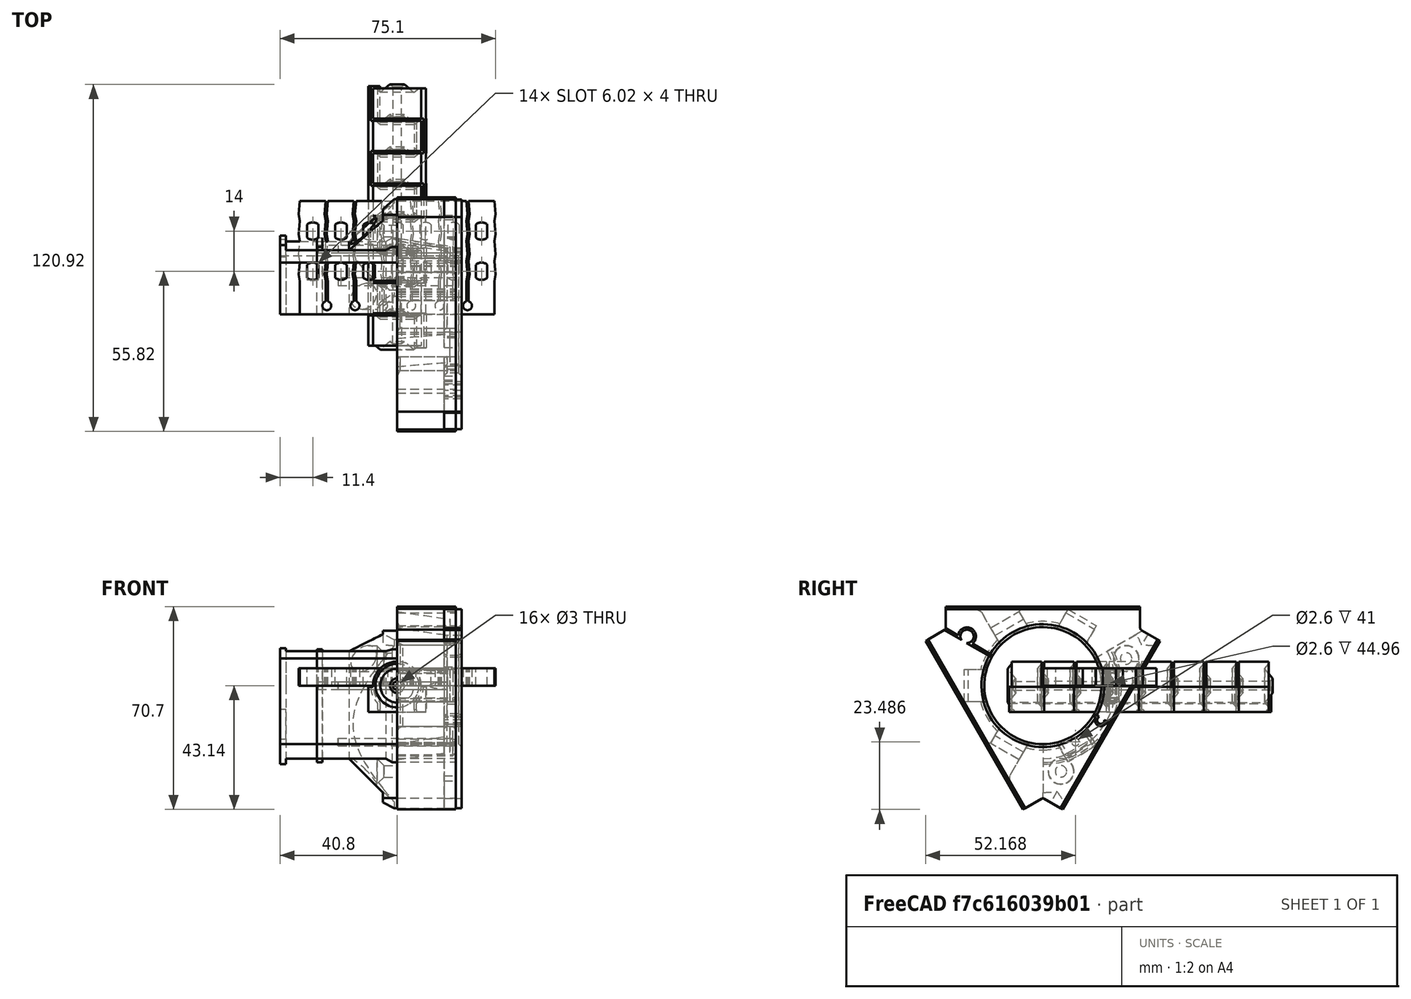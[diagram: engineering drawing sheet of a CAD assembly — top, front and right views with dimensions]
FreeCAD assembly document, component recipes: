
FREECAD ASSEMBLY — COMPONENT RECIPES ("BaseHingeModel_ver1.3_BandOnAxisBander")

This assembly document has 9 components, labeled P0..P8 below (a component is one placed body or linked part). 8 of them carry a construction recipe — the FreeCAD feature program that regenerates the part from scratch, quoted from this document or its linked companion documents; the rest are supplied as boundary geometry only. No exploded tour is included for this assembly.
NOTE — this tour is split across 2 documents so each fits a 32k-token context. This is document 1: the component sections continue in the remaining 1 document, each repeating the header above.
COMPONENT P0 — geometry summary ("Assembly"; no construction recipe available for this part):
  bounding box: 182.8 x 158.8 x 17.6 mm
  tessellated surface: 20,346 triangles
  volume: 11972621413014756431147097229976982929586403496314828412581110393578543582508654598538056830535573487008973004141558221594064665428114596506057430752296960 mm^3 (2342655092617214724371621224931003916189480584224963561102284116985405106658547483193773001758383925594768108753837361044603796868873288666810352140288% of its bounding box)
COMPONENT P1 — recipe-attached ("BaseHingePart", modeled in this document).
Construction recipe (the document's own serialized feature program — sketch geometry with constraints, then the solid features built on it; lengths are millimeters unless a unit is written):

FEATURE [Sketcher::SketchObject] Sketch007  label="RightCylinderScatch"
  FullyConstrained = true
  MapMode = 5
  Support = -> [XY_Plane002]
  expr: Constraints[10] = Spreadsheet.mmDiskHight
  expr: Constraints[11] = Spreadsheet.mmLedgeStep
  expr: Constraints[12] = Spreadsheet.mmLedgeStep * 2
  expr: Constraints[13] = Spreadsheet.mmLedgeStep
  expr: Constraints[14] = Spreadsheet.mmLedgeStep / 2
  expr: Constraints[16] = Spreadsheet.mmDiskLedge
  expr: Constraints[20] = Spreadsheet.mmDiskLedge * 2
  expr: Constraints[21] = Spreadsheet.mmDiskLedge
  expr: Constraints[34] = Spreadsheet.mmAirSpace / 2
  expr: Constraints[35] = Spreadsheet.mmLedgeStep / 2
  sketch-geometry (12):
    g0: LineSegment StartX=0 StartY=10.9 StartZ=0 EndX=0.84 EndY=10.9 EndZ=0
    g1: LineSegment StartX=0.84 StartY=10.9 StartZ=0 EndX=2.52 EndY=12.3 EndZ=0
    g2: LineSegment StartX=2.52 StartY=12.3 StartZ=0 EndX=5.88 EndY=9.5 EndZ=0
    g3: LineSegment StartX=5.88 StartY=9.5 StartZ=0 EndX=7.56 EndY=10.9 EndZ=0
    g4: LineSegment StartX=7.56 StartY=10.9 StartZ=0 EndX=8.4 EndY=10.9 EndZ=0
    g5: LineSegment StartX=5.88 StartY=-1 StartZ=0 EndX=2.52 EndY=1.8 EndZ=0
    g6: LineSegment StartX=2.52 StartY=1.8 StartZ=0 EndX=0.84 EndY=0.4 EndZ=0
    g7: LineSegment StartX=0.84 StartY=0.4 StartZ=0 EndX=0 EndY=0.4 EndZ=0
    g8: LineSegment StartX=0 StartY=0.4 StartZ=0 EndX=0 EndY=10.9 EndZ=0
    g9: LineSegment StartX=8.4 StartY=0.4 StartZ=0 EndX=7.56 EndY=0.4 EndZ=0
    g10: LineSegment StartX=7.56 StartY=0.4 StartZ=0 EndX=5.88 EndY=-1 EndZ=0
    g11: LineSegment StartX=8.4 StartY=10.9 StartZ=0 EndX=8.4 EndY=0.4 EndZ=0
  constraints (38):
    c: PointOnObject(g0,g-2)
    c: Horizontal(g0)
    c: Coincident(g0,g1)
    c: Coincident(g1,g2)
    c: Coincident(g2,g3)
    c: Coincident(g3,g4)
    c: Horizontal(g4)
    c: Coincident(g5,g6)
    c: Horizontal(g7)
    c: Coincident(g7,g8)
    c: DistanceY(g7,g0) = 10.5
    c: DistanceX(g0,g1) = 1.68
    c: DistanceX(g1,g2) = 3.36
    c: DistanceX(g2,g3) = 1.68
    c: DistanceX(g3,g4) = 0.84
    c: Coincident(g6,g7)
    c: DistanceY(g0,g1) = 1.4
    c: Equal(g0,g7)
    c: Equal(g1,g6)
    c: Coincident(g0,g8)
    c: DistanceY(g2,g1) = 2.8
    c: DistanceY(g2,g3) = 1.4
    c: Parallel(g2,g5)
    c: Coincident(g9,g10)
    c: Coincident(g10,g5)
    c: Parallel(g3,g10)
    c: Equal(g4,g9)
    c: Horizontal(g9)
    c: Vertical(g2,g5)
    c: Parallel(g1,g6)
    c: Vertical(g8)
    c: Coincident(g11,g4)
    c: Coincident(g11,g9)
    c: Vertical(g11)
    c: DistanceY(g-1,g7) = 0.4
    c: DistanceX(g-1,g0) = 0.84
    c: DistanceX(g-1,g0) = 0
    c: Vertical(g1,g5)
FEATURE [Sketcher::SketchObject] Sketch011  label="LeftCylinderScatch"
  FullyConstrained = true
  MapMode = 5
  Support = -> [XY_Plane]
  expr: Constraints[10] = Spreadsheet.mmLedgeStep
  expr: Constraints[11] = Spreadsheet.mmLedgeStep * 2
  expr: Constraints[12] = Spreadsheet.mmLedgeStep
  expr: Constraints[13] = Spreadsheet.mmLedgeStep / 2
  expr: Constraints[15] = Spreadsheet.mmDiskLedge
  expr: Constraints[19] = Spreadsheet.mmDiskLedge * 2
  expr: Constraints[20] = Spreadsheet.mmDiskLedge
  expr: Constraints[33] = Spreadsheet.mmAirSpace / 2
  expr: Constraints[34] = Spreadsheet.mmLedgeStep / 2
  expr: Constraints[9] = Spreadsheet.mmDiskHight
  sketch-geometry (12):
    g0: LineSegment StartX=0 StartY=-0.4 StartZ=0 EndX=0.84 EndY=-0.4 EndZ=0
    g1: LineSegment StartX=0.84 StartY=-0.4 StartZ=0 EndX=2.52 EndY=1 EndZ=0
    g2: LineSegment StartX=2.52 StartY=1 StartZ=0 EndX=5.88 EndY=-1.8 EndZ=0
    g3: LineSegment StartX=5.88 StartY=-1.8 StartZ=0 EndX=7.56 EndY=-0.4 EndZ=0
    g4: LineSegment StartX=7.56 StartY=-0.4 StartZ=0 EndX=8.4 EndY=-0.4 EndZ=0
    g5: LineSegment StartX=5.88 StartY=-12.3 StartZ=0 EndX=2.52 EndY=-9.5 EndZ=0
    g6: LineSegment StartX=2.52 StartY=-9.5 StartZ=0 EndX=0.84 EndY=-10.9 EndZ=0
    g7: LineSegment StartX=0.84 StartY=-10.9 StartZ=0 EndX=0 EndY=-10.9 EndZ=0
    g8: LineSegment StartX=0 StartY=-10.9 StartZ=0 EndX=0 EndY=-0.4 EndZ=0
    g9: LineSegment StartX=8.4 StartY=-10.9 StartZ=0 EndX=7.56 EndY=-10.9 EndZ=0
    g10: LineSegment StartX=7.56 StartY=-10.9 StartZ=0 EndX=5.88 EndY=-12.3 EndZ=0
    g11: LineSegment StartX=8.4 StartY=-0.4 StartZ=0 EndX=8.4 EndY=-10.9 EndZ=0
  constraints (36):
    c: Horizontal(g0)
    c: Coincident(g0,g1)
    c: Coincident(g1,g2)
    c: Coincident(g2,g3)
    c: Coincident(g3,g4)
    c: Horizontal(g4)
    c: Coincident(g5,g6)
    c: Horizontal(g7)
    c: Coincident(g7,g8)
    c: DistanceY(g7,g0) = 10.5
    c: DistanceX(g0,g1) = 1.68
    c: DistanceX(g1,g2) = 3.36
    c: DistanceX(g2,g3) = 1.68
    c: DistanceX(g3,g4) = 0.84
    c: Coincident(g6,g7)
    c: DistanceY(g0,g1) = 1.4
    c: Equal(g0,g7)
    c: Equal(g1,g6)
    c: Coincident(g0,g8)
    c: DistanceY(g2,g1) = 2.8
    c: DistanceY(g2,g3) = 1.4
    c: Parallel(g2,g5)
    c: Coincident(g9,g10)
    c: Coincident(g10,g5)
    c: Parallel(g3,g10)
    c: Equal(g4,g9)
    c: Horizontal(g9)
    c: Vertical(g2,g5)
    c: Parallel(g1,g6)
    c: Vertical(g8)
    c: Coincident(g11,g4)
    c: Coincident(g11,g9)
    c: Vertical(g11)
    c: DistanceY(g0,g-1) = 0.4
    c: DistanceX(g-1,g0) = 0.84
    c: DistanceX(g-1,g0) = 0
FEATURE [PartDesign::Revolution] Revolution  label="RightCylinderRevolution"
  Angle = 360
  Axis = (0,1,0)
  Base = (0,0,0)
  Profile = -> Sketch007
  ReferenceAxis = -> Sketch007 [V_Axis]
  Reversed = true
FEATURE [PartDesign::Revolution] Revolution004  label="LeftCylinderRevolution"
  Angle = 360
  Axis = (0,1,0)
  Base = (0,0,0)
  Profile = -> Sketch011
  ReferenceAxis = -> Sketch011 [V_Axis]
  Reversed = true
FEATURE [Sketcher::SketchObject] Sketch013  label="RightCylinderAxisHoleScatch"
  AttachmentOffset = pos=(0,0,1) rot=(0,0,1;0rad)
  FullyConstrained = true
  MapMode = 5
  Placement = pos=(0,-1,-2e-16) rot=(1,0,0;1.5708rad)
  Support = -> [XZ_Plane002]
  expr: .AttachmentOffset.Base.z = Spreadsheet.mmDiskLedge - Spreadsheet.mmAirSpace / 2
  expr: Constraints[1] = Spreadsheet.mmHoleRadius * 2
  sketch-geometry (1):
    g0: Circle CenterX=0 CenterY=0 CenterZ=0 NormalX=0 NormalY=0 NormalZ=1 AngleXU=0 Radius=1.5
  constraints (2):
    c: Coincident(g0,g-1)
    c: Diameter(g0) = 3
FEATURE [PartDesign::Pocket] Pocket001  label="RightCylinderAxisHole"
  BaseFeature = -> Revolution
  Direction = (0,1,2e-16)
  Length = 23.8
  Length2 = 5
  Profile = -> Sketch013
  ReferenceAxis = -> Sketch013 [N_Axis]
  Type = 0
  expr: Length = 2 * Spreadsheet.mmDiskHight + 2 * Spreadsheet.mmDiskLedge
FEATURE [Sketcher::SketchObject] Sketch014  label="LeftCylinderAxisHoleScatch"
  AttachmentOffset = pos=(0,0,-1) rot=(0,0,1;0rad)
  FullyConstrained = true
  MapMode = 5
  Placement = pos=(0,1,2e-16) rot=(1,0,0;1.5708rad)
  Support = -> [XZ_Plane]
  expr: .AttachmentOffset.Base.z = -(Spreadsheet.mmDiskLedge - Spreadsheet.mmAirSpace / 2)
  expr: Constraints[1] = Spreadsheet.mmHoleRadius * 2
  sketch-geometry (1):
    g0: Circle CenterX=0 CenterY=0 CenterZ=0 NormalX=0 NormalY=0 NormalZ=1 AngleXU=0 Radius=1.5
  constraints (2):
    c: Coincident(g0,g-1)
    c: Diameter(g0) = 3
FEATURE [PartDesign::Pocket] Pocket002  label="LeftCylinderAxisHole"
  BaseFeature = -> Revolution004
  Direction = (0,1,2e-16)
  Length = 21
  Length2 = 5
  Profile = -> Sketch014
  ReferenceAxis = -> Sketch014 [N_Axis]
  Reversed = true
  Type = 0
  expr: Length = Spreadsheet.mmDiskHight * 2
FEATURE [Sketcher::SketchObject] Sketch023  label="RightCylinderConnectedWingScatch"
  AttachmentOffset = pos=(0,0,-0.4) rot=(0,0,1;0rad)
  FullyConstrained = false
  MapMode = 5
  Placement = pos=(0,0.4,1e-16) rot=(1,0,0;1.5708rad)
  Support = -> [XZ_Plane002]
  expr: .AttachmentOffset.Base.z = -Spreadsheet.mmAirSpace / 2
  expr: Constraints[11] = Spreadsheet.mmHingeRadius + Spreadsheet.mmAirSpace
  expr: Constraints[17] = Spreadsheet.mmHingeRadius + Spreadsheet.mmAirSpace
  expr: Constraints[4] = Spreadsheet.mmHingeRadius * 2
  expr: Constraints[7] = Spreadsheet.mmHingeRadius / 5
  expr: Constraints[8] = Spreadsheet.mmAirSpace / 2
  sketch-geometry (9):
    g0: LineSegment StartX=-5.9397 StartY=-9.2 StartZ=0 EndX=10.0705 EndY=-9.2 EndZ=0
    g1: LineSegment StartX=10.0705 StartY=-9.2 StartZ=0 EndX=10.0705 EndY=-0.4 EndZ=0
    g2: LineSegment StartX=10.0705 StartY=-0.4 StartZ=0 EndX=8.39047 EndY=-0.4 EndZ=0
    g3: ArcOfCircle CenterX=0 CenterY=9e-16 CenterZ=0 NormalX=0 NormalY=0 NormalZ=1 AngleXU=0 Radius=8.4 StartAngle=3.92699 EndAngle=6.23555
    g4: LineSegment StartX=-10.8949 StartY=25.2528 StartZ=0 EndX=-10.8949 EndY=-29.472 EndZ=0
    g5: LineSegment StartX=0 StartY=0 StartZ=0 EndX=8.39047 EndY=-0.4 EndZ=0
    g6: LineSegment StartX=-5.9397 StartY=-5.9397 StartZ=0 EndX=-5.9397 EndY=-9.2 EndZ=0
    g7: LineSegment StartX=0 StartY=9e-16 StartZ=0 EndX=-20.2547 EndY=-20.2547 EndZ=0
    g8: LineSegment StartX=-5.9397 StartY=-5.9397 StartZ=0 EndX=-5.9397 EndY=-9.42884 EndZ=0
  constraints (24):
    c: Coincident(g0,g1)
    c: Vertical(g1)
    c: Horizontal(g2)
    c: Vertical(g4)
    c: Diameter(g3) = 16.8
    c: Coincident(g2,g1)
    c: Coincident(g5,g2)
    c: DistanceX(g2,g2) = 1.68
    c: DistanceY(g1,g-1) = 0.4
    c: Coincident(g3,g6)
    c: Coincident(g3,g2)
    c: DistanceY(g0,g3) = 9.2
    c: PointOnObject(g3,g7)
    c: Coincident(g7,g3)
    c: Angle(g-2,g7) = 2.35619
    c: PointOnObject(g3,g-2)
    c: Horizontal(g0)
    c: DistanceY(g0,g-1) = 9.2
    c: Vertical(g8)
    c: PointOnObject(g8,g7)
    c: PointOnObject(g8,g3)
    c: PointOnObject(g6,g8)
    c: PointOnObject(g0,g8)
    c: PointOnObject(g6,g0)
FEATURE [PartDesign::Pad] Pad008  label="RightCylinderConnectedWingBody"
  BaseFeature = -> Pocket001
  Direction = (0,-1,-2e-16)
  Length = 10.5
  Length2 = 10
  Profile = -> Sketch023
  ReferenceAxis = -> Sketch023 [N_Axis]
  Reversed = true
  Type = 0
  expr: Length = Spreadsheet.mmDiskHight
FEATURE [Sketcher::SketchObject] Sketch024  label="RightCylinderDisconnectedWingScatch"
  AttachmentOffset = pos=(0,0,0.4) rot=(0,0,1;0rad)
  FullyConstrained = false
  MapMode = 5
  Placement = pos=(0,-0.4,-1e-16) rot=(1,0,0;1.5708rad)
  Support = -> [XZ_Plane002]
  expr: .AttachmentOffset.Base.z = Spreadsheet.mmAirSpace / 2
  expr: Constraints[10] = Spreadsheet.mmHingeRadius * 6 / 5
  expr: Constraints[14] = (Spreadsheet.mmHingeRadius + Spreadsheet.mmAirSpace) * 2
  expr: Constraints[18] = Spreadsheet.mmAirSpace
  expr: Constraints[26] = Spreadsheet.mmAirSpace
  expr: Constraints[29] = Spreadsheet.mmHingeRadius * 2
  expr: Constraints[2] = (Spreadsheet.mmHingeRadius + Spreadsheet.mmAirSpace) * 2
  expr: Constraints[8] = Spreadsheet.mmHingeRadius + Spreadsheet.mmAirSpace
  expr: Constraints[9] = Spreadsheet.mmAirSpace / 2
  sketch-geometry (12):
    g0: Circle CenterX=0 CenterY=0 CenterZ=0 NormalX=0 NormalY=0 NormalZ=1 AngleXU=0 Radius=9.2
    g1: LineSegment StartX=-5.9397 StartY=-5.9397 StartZ=0 EndX=-5.9397 EndY=-9.59435 EndZ=0
    g2: LineSegment StartX=-10.08 StartY=-0.4 StartZ=0 EndX=-10.08 EndY=-9.2 EndZ=0
    g3: LineSegment StartX=-10.08 StartY=-9.2 StartZ=0 EndX=-5.9397 EndY=-9.2 EndZ=0
    g4: LineSegment StartX=-6.7397 StartY=-8.4 StartZ=0 EndX=-6.7397 EndY=-6.26231 EndZ=0
    g5: LineSegment StartX=-9.1913 StartY=-0.4 StartZ=0 EndX=-10.08 EndY=-0.4 EndZ=0
    g6: LineSegment StartX=0 StartY=0 StartZ=0 EndX=-7.18968 EndY=-7.18968 EndZ=0
    g7: ArcOfCircle CenterX=0 CenterY=0 CenterZ=0 NormalX=0 NormalY=0 NormalZ=1 AngleXU=0 Radius=9.2 StartAngle=3.18508 EndAngle=3.89029
    g8: LineSegment StartX=-6.7397 StartY=-9.55843 StartZ=0 EndX=-6.7397 EndY=-4.9559 EndZ=0
    g9: LineSegment StartX=-6.7397 StartY=-8.4 StartZ=0 EndX=-5.9397 EndY=-8.4 EndZ=0
    g10: LineSegment StartX=-5.9397 StartY=-8.4 StartZ=0 EndX=-5.9397 EndY=-9.2 EndZ=0
    g11: Circle CenterX=0 CenterY=0 CenterZ=0 NormalX=0 NormalY=0 NormalZ=1 AngleXU=0 Radius=8.4
  constraints (33):
    c: Coincident(g0,g-1)
    c: Vertical(g1)
    c: Diameter(g0) = 18.4
    c: Vertical(g2)
    c: Coincident(g2,g3)
    c: Horizontal(g3)
    c: Coincident(g5,g2)
    c: Horizontal(g5)
    c: DistanceY(g2,g-1) = 9.2
    c: DistanceY(g2,g-1) = 0.4
    c: DistanceX(g2,g0) = 10.08
    c: Coincident(g6,g0)
    c: Angle(g-2,g6) = 2.35619
    c: Coincident(g7,g0)
    c: Diameter(g7) = 18.4
    c: Coincident(g7,g4)
    c: Coincident(g7,g5)
    c: Vertical(g8)
    c: DistanceX(g8,g1) = 0.8
    c: Coincident(g4,g9)
    c: PointOnObject(g9,g1)
    c: Horizontal(g9)
    c: Coincident(g9,g10)
    c: PointOnObject(g10,g1)
    c: PointOnObject(g3,g1)
    c: PointOnObject(g10,g3)
    c: DistanceY(g3,g9) = 0.8
    c: PointOnObject(g4,g8)
    c: Coincident(g11,g7)
    c: Diameter(g11) = 16.8
    c: PointOnObject(g1,g11)
    c: PointOnObject(g1,g6)
    c: PointOnObject(g4,g8)
FEATURE [PartDesign::Pad] Pad009  label="RightCylinderDisconnectedWingBody"
  BaseFeature = -> Pad008
  Direction = (0,-1,-2e-16)
  Length = 12.1
  Length2 = 10
  Profile = -> Sketch024
  ReferenceAxis = -> Sketch024 [N_Axis]
  Reversed = true
  Type = 0
  expr: Length = Spreadsheet.mmDiskHight + Spreadsheet.mmAirSpace * 2
FEATURE [Sketcher::SketchObject] Sketch025  label="LeftCylinderConnectedWingScatch"
  AttachmentOffset = pos=(0,0,0.4) rot=(0,0,1;0rad)
  FullyConstrained = false
  MapMode = 5
  Placement = pos=(0,-0.4,-1e-16) rot=(1,0,0;1.5708rad)
  Support = -> [XZ_Plane]
  expr: .AttachmentOffset.Base.z = Spreadsheet.mmAirSpace / 2
  expr: Constraints[10] = Spreadsheet.mmAirSpace / 2
  expr: Constraints[11] = Spreadsheet.mmHingeRadius + Spreadsheet.mmAirSpace
  expr: Constraints[15] = Spreadsheet.mmHingeRadius * 2
  expr: Constraints[2] = Spreadsheet.mmHingeRadius * 2
  expr: Constraints[9] = Spreadsheet.mmHingeRadius * 6 / 5
  sketch-geometry (8):
    g0: LineSegment StartX=0 StartY=0 StartZ=0 EndX=8.8497 EndY=-8.8497 EndZ=0
    g1: Circle CenterX=0 CenterY=0 CenterZ=0 NormalX=0 NormalY=0 NormalZ=1 AngleXU=0 Radius=8.4
    g2: LineSegment StartX=-10.08 StartY=-0.4 StartZ=0 EndX=-10.08 EndY=-9.2 EndZ=0
    g3: LineSegment StartX=-10.08 StartY=-9.2 StartZ=0 EndX=5.9397 EndY=-9.2 EndZ=0
    g4: LineSegment StartX=5.9397 StartY=-9.2 StartZ=0 EndX=5.9397 EndY=-5.9397 EndZ=0
    g5: LineSegment StartX=-8.39047 StartY=-0.4 StartZ=0 EndX=-10.08 EndY=-0.4 EndZ=0
    g6: ArcOfCircle CenterX=0 CenterY=0 CenterZ=0 NormalX=0 NormalY=0 NormalZ=1 AngleXU=0 Radius=8.4 StartAngle=3.18923 EndAngle=5.49779
    g7: LineSegment StartX=5.9397 StartY=-5.9397 StartZ=0 EndX=5.9397 EndY=-9.58153 EndZ=0
  constraints (24):
    c: Coincident(g0,g-1)
    c: Coincident(g1,g0)
    c: Diameter(g1) = 16.8
    c: Vertical(g2)
    c: Coincident(g2,g3)
    c: Horizontal(g3)
    c: Coincident(g5,g2)
    c: Horizontal(g5)
    c: PointOnObject(g5,g1)
    c: DistanceX(g2,g0) = 10.08
    c: DistanceY(g2,g-1) = 0.4
    c: DistanceY(g2,g-1) = 9.2
    c: Angle(g0,g-2) = 2.35619
    c: PointOnObject(g4,g0)
    c: Coincident(g6,g0)
    c: Diameter(g6) = 16.8
    c: Coincident(g6,g5)
    c: Coincident(g6,g4)
    c: Vertical(g7)
    c: PointOnObject(g7,g1)
    c: PointOnObject(g7,g0)
    c: PointOnObject(g4,g7)
    c: PointOnObject(g3,g7)
    c: PointOnObject(g4,g3)
FEATURE [PartDesign::Pad] Pad010  label="LeftCylinderConnectedWingBody"
  BaseFeature = -> Pocket002
  Direction = (0,-1,-2e-16)
  Length = 10.5
  Length2 = 10
  Profile = -> Sketch025
  ReferenceAxis = -> Sketch025 [N_Axis]
  Type = 0
  expr: Length = Spreadsheet.mmDiskHight
FEATURE [Sketcher::SketchObject] Sketch026  label="LeftCylinderDisconnectedWingScatch"
  AttachmentOffset = pos=(0,0,-0.4) rot=(0,0,1;0rad)
  FullyConstrained = false
  MapMode = 5
  Placement = pos=(0,0.4,1e-16) rot=(1,0,0;1.5708rad)
  Support = -> [XZ_Plane]
  expr: .AttachmentOffset.Base.z = -Spreadsheet.mmAirSpace / 2
  expr: Constraints[10] = Spreadsheet.mmHingeRadius + Spreadsheet.mmAirSpace
  expr: Constraints[16] = Spreadsheet.mmAirSpace
  expr: Constraints[18] = (Spreadsheet.mmHingeRadius + Spreadsheet.mmAirSpace) * 2
  expr: Constraints[26] = Spreadsheet.mmAirSpace
  expr: Constraints[29] = Spreadsheet.mmHingeRadius * 2
  expr: Constraints[2] = (Spreadsheet.mmHingeRadius + Spreadsheet.mmAirSpace) * 2
  expr: Constraints[8] = Spreadsheet.mmAirSpace / 2
  expr: Constraints[9] = Spreadsheet.mmHingeRadius / 5 * 6
  sketch-geometry (12):
    g0: LineSegment StartX=0 StartY=0 StartZ=0 EndX=9.28474 EndY=-9.28474 EndZ=0
    g1: ArcOfCircle CenterX=0 CenterY=0 CenterZ=0 NormalX=0 NormalY=0 NormalZ=1 AngleXU=0 Radius=9.2 StartAngle=5.53449 EndAngle=6.23969
    g2: LineSegment StartX=9.1913 StartY=-0.4 StartZ=0 EndX=10.08 EndY=-0.4 EndZ=0
    g3: LineSegment StartX=10.08 StartY=-0.4 StartZ=0 EndX=10.08 EndY=-9.2 EndZ=0
    g4: LineSegment StartX=10.08 StartY=-9.2 StartZ=0 EndX=5.9397 EndY=-9.2 EndZ=0
    g5: LineSegment StartX=6.7397 StartY=-8.4 StartZ=0 EndX=6.7397 EndY=-6.26231 EndZ=0
    g6: LineSegment StartX=5.9397 StartY=-5.9397 StartZ=0 EndX=5.9397 EndY=-9.17966 EndZ=0
    g7: LineSegment StartX=6.7397 StartY=-5.451 StartZ=0 EndX=6.7397 EndY=-9.15329 EndZ=0
    g8: Circle CenterX=0 CenterY=0 CenterZ=0 NormalX=0 NormalY=0 NormalZ=1 AngleXU=0 Radius=9.2
    g9: LineSegment StartX=6.7397 StartY=-8.4 StartZ=0 EndX=5.9397 EndY=-8.4 EndZ=0
    g10: LineSegment StartX=5.9397 StartY=-8.4 StartZ=0 EndX=5.9397 EndY=-9.2 EndZ=0
    g11: Circle CenterX=0 CenterY=0 CenterZ=0 NormalX=0 NormalY=0 NormalZ=1 AngleXU=0 Radius=8.4
  constraints (33):
    c: Coincident(g0,g-1)
    c: Coincident(g1,g0)
    c: Diameter(g1) = 18.4
    c: Horizontal(g2)
    c: Coincident(g2,g3)
    c: Vertical(g3)
    c: Coincident(g3,g4)
    c: Horizontal(g4)
    c: DistanceY(g2,g-1) = 0.4
    c: DistanceX(g-1,g2) = 10.08
    c: DistanceY(g3,g-1) = 9.2
    c: Angle(g0,g-2) = 2.35619
    c: Coincident(g1,g2)
    c: Coincident(g1,g5)
    c: Vertical(g6)
    c: Vertical(g7)
    c: DistanceX(g6,g7) = 0.8
    c: Coincident(g8,g1)
    c: Diameter(g8) = 18.4
    c: PointOnObject(g5,g7)
    c: Coincident(g5,g9)
    c: PointOnObject(g9,g6)
    c: Horizontal(g9)
    c: Coincident(g9,g10)
    c: PointOnObject(g10,g6)
    c: PointOnObject(g4,g6)
    c: DistanceY(g4,g9) = 0.8
    c: PointOnObject(g10,g4)
    c: Coincident(g11,g1)
    c: Diameter(g11) = 16.8
    c: PointOnObject(g6,g11)
    c: PointOnObject(g6,g0)
    c: PointOnObject(g1,g7)
FEATURE [PartDesign::Pad] Pad011  label="LeftCylinderDisconnectedWingBody"
  BaseFeature = -> Pad010
  Direction = (0,-1,-2e-16)
  Length = 12.1
  Length2 = 10
  Profile = -> Sketch026
  ReferenceAxis = -> Sketch026 [N_Axis]
  Type = 0
  expr: Length = Spreadsheet.mmDiskHight + Spreadsheet.mmAirSpace * 2
FEATURE [Sketcher::SketchObject] Sketch046  label="LeftCylinderSeparatorScatch"
  AttachmentOffset = pos=(0,0,-0.4) rot=(0,0,1;0rad)
  FullyConstrained = false
  MapMode = 5
  Placement = pos=(0,0.4,1e-16) rot=(1,0,0;1.5708rad)
  Support = -> [XZ_Plane]
  expr: .AttachmentOffset.Base.z = -Spreadsheet.mmAirSpace / 2
  expr: Constraints[14] = Spreadsheet.mmAirSpace
  expr: Constraints[15] = Spreadsheet.mmHingeRadius * 2
  expr: Constraints[2] = Spreadsheet.mmHingeRadius + Spreadsheet.mmAirSpace
  expr: Constraints[6] = Spreadsheet.mmAirSpace
  expr: Constraints[7] = (Spreadsheet.mmHingeRadius + Spreadsheet.mmAirSpace) * 2
  sketch-geometry (9):
    g0: LineSegment StartX=0 StartY=0 StartZ=0 EndX=9.28922 EndY=-9.28922 EndZ=0
    g1: LineSegment StartX=6.7397 StartY=-9.2 StartZ=0 EndX=5.9397 EndY=-9.2 EndZ=0
    g2: LineSegment StartX=6.7397 StartY=-8.4 StartZ=0 EndX=6.7397 EndY=-9.2 EndZ=0
    g3: LineSegment StartX=5.9397 StartY=-5.9397 StartZ=0 EndX=5.9397 EndY=-8.88748 EndZ=0
    g4: LineSegment StartX=6.7397 StartY=-5.40605 StartZ=0 EndX=6.7397 EndY=-8.88997 EndZ=0
    g5: Circle CenterX=0 CenterY=0 CenterZ=0 NormalX=0 NormalY=0 NormalZ=1 AngleXU=0 Radius=9.2
    g6: LineSegment StartX=6.7397 StartY=-8.4 StartZ=0 EndX=5.9397 EndY=-8.4 EndZ=0
    g7: LineSegment StartX=5.9397 StartY=-8.4 StartZ=0 EndX=5.9397 EndY=-9.2 EndZ=0
    g8: Circle CenterX=0 CenterY=0 CenterZ=0 NormalX=0 NormalY=0 NormalZ=1 AngleXU=0 Radius=8.4
  constraints (23):
    c: Coincident(g0,g-1)
    c: Horizontal(g1)
    c: DistanceY(g1,g-1) = 9.2
    c: Angle(g0,g-2) = 2.35619
    c: Vertical(g3)
    c: Vertical(g4)
    c: DistanceX(g3,g4) = 0.8
    c: Diameter(g5) = 18.4
    c: PointOnObject(g2,g4)
    c: Coincident(g2,g6)
    c: PointOnObject(g6,g3)
    c: Horizontal(g6)
    c: Coincident(g6,g7)
    c: PointOnObject(g7,g3)
    c: DistanceY(g1,g6) = 0.8
    c: Diameter(g8) = 16.8
    c: PointOnObject(g3,g8)
    c: PointOnObject(g3,g0)
    c: PointOnObject(g1,g4)
    c: Coincident(g2,g1)
    c: Coincident(g0,g8)
    c: Coincident(g0,g5)
    c: Coincident(g7,g1)
FEATURE [PartDesign::Pocket] Pocket004  label="LeftCylinderSeparator"
  BaseFeature = -> Pad011
  Direction = (0,1,2e-16)
  Length = 10.5
  Length2 = 5
  Profile = -> Sketch046
  ReferenceAxis = -> Sketch046 [N_Axis]
  Reversed = true
  Type = 0
  expr: Length = Spreadsheet.mmDiskHight
FEATURE [PartDesign::Body] Body  label="LeftCylinder"
  Group = -> [Sketch011,Revolution004,Sketch014,Pocket002,Sketch025,Pad010,Sketch026,Pad011,Sketch046,Pocket004]
  Origin = -> Origin
  Tip = -> Pocket004
FEATURE [Sketcher::SketchObject] Sketch047  label="RightCylinderSeparatorScatch"
  AttachmentOffset = pos=(0,0,0.4) rot=(0,0,1;0rad)
  FullyConstrained = false
  MapMode = 5
  Placement = pos=(0,-0.4,-1e-16) rot=(1,0,0;1.5708rad)
  Support = -> [XZ_Plane002]
  expr: .AttachmentOffset.Base.z = Spreadsheet.mmAirSpace / 2
  expr: Constraints[15] = Spreadsheet.mmAirSpace
  expr: Constraints[17] = Spreadsheet.mmHingeRadius * 2
  expr: Constraints[2] = (Spreadsheet.mmHingeRadius + Spreadsheet.mmAirSpace) * 2
  expr: Constraints[4] = Spreadsheet.mmHingeRadius + Spreadsheet.mmAirSpace
  expr: Constraints[8] = Spreadsheet.mmAirSpace
  sketch-geometry (9):
    g0: Circle CenterX=0 CenterY=0 CenterZ=0 NormalX=0 NormalY=0 NormalZ=1 AngleXU=0 Radius=9.2
    g1: LineSegment StartX=-5.9397 StartY=-5.9397 StartZ=0 EndX=-5.9397 EndY=-9.59435 EndZ=0
    g2: LineSegment StartX=-6.7397 StartY=-9.2 StartZ=0 EndX=-5.9397 EndY=-9.2 EndZ=0
    g3: LineSegment StartX=0 StartY=0 StartZ=0 EndX=-7.19425 EndY=-7.19425 EndZ=0
    g4: LineSegment StartX=-6.7397 StartY=-9.55843 StartZ=0 EndX=-6.7397 EndY=-4.9559 EndZ=0
    g5: LineSegment StartX=-6.7397 StartY=-8.4 StartZ=0 EndX=-5.9397 EndY=-8.4 EndZ=0
    g6: LineSegment StartX=-5.9397 StartY=-8.4 StartZ=0 EndX=-5.9397 EndY=-9.2 EndZ=0
    g7: Circle CenterX=0 CenterY=0 CenterZ=0 NormalX=0 NormalY=0 NormalZ=1 AngleXU=0 Radius=8.4
    g8: LineSegment StartX=-6.7397 StartY=-8.4 StartZ=0 EndX=-6.7397 EndY=-9.2 EndZ=0
  constraints (24):
    c: Coincident(g0,g-1)
    c: Vertical(g1)
    c: Diameter(g0) = 18.4
    c: Horizontal(g2)
    c: DistanceY(g2,g-1) = 9.2
    c: Coincident(g3,g0)
    c: Angle(g-2,g3) = 2.35619
    c: Vertical(g4)
    c: DistanceX(g4,g1) = 0.8
    c: PointOnObject(g5,g1)
    c: Horizontal(g5)
    c: Coincident(g5,g6)
    c: PointOnObject(g6,g1)
    c: PointOnObject(g2,g1)
    c: PointOnObject(g6,g2)
    c: DistanceY(g2,g5) = 0.8
    c: PointOnObject(g5,g4)
    c: Diameter(g7) = 16.8
    c: PointOnObject(g1,g7)
    c: PointOnObject(g1,g3)
    c: PointOnObject(g2,g4)
    c: Coincident(g8,g5)
    c: Coincident(g8,g2)
    c: Coincident(g0,g7)
FEATURE [PartDesign::Pocket] Pocket005  label="RightCylinderSeparator"
  BaseFeature = -> Pad009
  Direction = (0,1,2e-16)
  Length = 10.5
  Length2 = 5
  Profile = -> Sketch047
  ReferenceAxis = -> Sketch047 [N_Axis]
  Type = 0
  expr: Length = Spreadsheet.mmDiskHight
FEATURE [PartDesign::Body] Body001  label="RightCylinder"
  Group = -> [Sketch007,Revolution,Sketch013,Pocket001,Sketch023,Pad008,Sketch024,Pad009,Sketch047,Pocket005]
  Origin = -> Origin002
  Tip = -> Pocket005
COMPONENT P2 — recipe-attached ("BeamFixatoPart", modeled in this document).
Construction recipe (the document's own serialized feature program — sketch geometry with constraints, then the solid features built on it; lengths are millimeters unless a unit is written):

FEATURE [Sketcher::SketchObject] Sketch022  label="FixatorBodySketch"
  FullyConstrained = false
  MapMode = 5
  Support = -> [XY_Plane005]
  expr: Constraints[143] = Spreadsheet.mmCellWall
  expr: Constraints[144] = Spreadsheet.mmCellWall
  expr: Constraints[145] = Spreadsheet.mmCellWall
  expr: Constraints[146] = Spreadsheet.mmCellWidth
  expr: Constraints[147] = Spreadsheet.mmCellWidth
  expr: Constraints[148] = Spreadsheet.mmCellWidth
  expr: Constraints[169] = Spreadsheet.mmCommonBaseLenght
  expr: Constraints[170] = Spreadsheet.mmToothStep
  expr: Constraints[171] = Spreadsheet.mmToothStep
  expr: Constraints[172] = Spreadsheet.mmToothStep
  expr: Constraints[173] = Spreadsheet.mmToothStep
  expr: Constraints[174] = Spreadsheet.mmToothStep
  expr: Constraints[183] = Spreadsheet.mmCellWall * 3
  expr: Constraints[184] = Spreadsheet.mmCellWall * 3
  expr: Constraints[185] = Spreadsheet.mmCellWall * 3
  expr: Constraints[186] = Spreadsheet.mmCellWall * 3
  expr: Constraints[425] = Spreadsheet.mmFirstCircleArcToBase
  expr: Constraints[435] = Spreadsheet.mmCellWall / 2
  expr: Constraints[464] = Spreadsheet.mmCellWidth + Spreadsheet.mmCellWall
  expr: Constraints[5] = Spreadsheet.mmBaseWidth
  expr: Constraints[6] = Spreadsheet.mmBaseEnd
  sketch-geometry (155):
    g0: LineSegment StartX=-33.9 StartY=0 StartZ=0 EndX=-33.9 EndY=39.5 EndZ=0
    g1: LineSegment StartX=-33.9 StartY=39.5 StartZ=0 EndX=33.9 EndY=39.5 EndZ=0
    g2: LineSegment StartX=33.9 StartY=39.5 StartZ=0 EndX=33.9 EndY=0 EndZ=0
    g3: LineSegment StartX=-73.1099 StartY=25.5 StartZ=0 EndX=65.6354 EndY=25.5 EndZ=0
    g4: LineSegment StartX=-33.9 StartY=0 StartZ=0 EndX=-33.9 EndY=11.5 EndZ=0
    g5: LineSegment StartX=-33.9 StartY=11.5 StartZ=0 EndX=-34.3 EndY=13.9 EndZ=0
    g6: LineSegment StartX=-34.3 StartY=13.9 StartZ=0 EndX=-33.9 EndY=18.5 EndZ=0
    g7: LineSegment StartX=-33.9 StartY=18.5 StartZ=0 EndX=-34.3 EndY=20.9 EndZ=0
    g8: LineSegment StartX=-34.3 StartY=20.9 StartZ=0 EndX=-33.9 EndY=25.5 EndZ=0
    g9: LineSegment StartX=-33.9 StartY=25.5 StartZ=0 EndX=-34.3 EndY=27.9 EndZ=0
    g10: LineSegment StartX=-34.3 StartY=27.9 StartZ=0 EndX=-33.9 EndY=32.5 EndZ=0
    g11: LineSegment StartX=-33.9 StartY=32.5 StartZ=0 EndX=-34.3 EndY=34.9 EndZ=0
    g12: LineSegment StartX=-34.3 StartY=34.9 StartZ=0 EndX=-33.9 EndY=39.5 EndZ=0
    g13: LineSegment StartX=-33.9 StartY=39.5 StartZ=0 EndX=-24.9 EndY=39.5 EndZ=0
    g14: LineSegment StartX=-24.9 StartY=39.5 StartZ=0 EndX=-25.3 EndY=34.9 EndZ=0
    g15: LineSegment StartX=-25.3 StartY=34.9 StartZ=0 EndX=-24.9 EndY=32.5 EndZ=0
    g16: LineSegment StartX=-24.9 StartY=32.5 StartZ=0 EndX=-25.3 EndY=27.9 EndZ=0
    g17: LineSegment StartX=-25.3 StartY=27.9 StartZ=0 EndX=-24.9 EndY=25.5 EndZ=0
    g18: LineSegment StartX=-24.9 StartY=25.5 StartZ=0 EndX=-25.3 EndY=20.9 EndZ=0
    g19: LineSegment StartX=-25.3 StartY=20.9 StartZ=0 EndX=-24.9 EndY=18.5 EndZ=0
    g20: LineSegment StartX=-24.9 StartY=18.5 StartZ=0 EndX=-25.3 EndY=13.9 EndZ=0
    g21: LineSegment StartX=-25.3 StartY=13.9 StartZ=0 EndX=-24.9 EndY=11.5 EndZ=0
    g22: LineSegment StartX=-24.9 StartY=11.5 StartZ=0 EndX=-24.9 EndY=4.5 EndZ=0
    g23: LineSegment StartX=-24.1 StartY=4.5 StartZ=0 EndX=-24.1 EndY=11.5 EndZ=0
    g24: LineSegment StartX=-24.1 StartY=11.5 StartZ=0 EndX=-24.5 EndY=13.9 EndZ=0
    g25: LineSegment StartX=-24.5 StartY=13.9 StartZ=0 EndX=-24.1 EndY=18.5 EndZ=0
    g26: LineSegment StartX=-24.1 StartY=18.5 StartZ=0 EndX=-24.5 EndY=20.9 EndZ=0
    g27: LineSegment StartX=-24.5 StartY=20.9 StartZ=0 EndX=-24.1 EndY=25.5 EndZ=0
    g28: LineSegment StartX=-24.1 StartY=25.5 StartZ=0 EndX=-24.5 EndY=27.9 EndZ=0
    g29: LineSegment StartX=-24.5 StartY=27.9 StartZ=0 EndX=-24.1 EndY=32.5 EndZ=0
    g30: LineSegment StartX=-24.1 StartY=32.5 StartZ=0 EndX=-24.5 EndY=34.9 EndZ=0
    g31: LineSegment StartX=-24.5 StartY=34.9 StartZ=0 EndX=-24.1 EndY=39.5 EndZ=0
    g32: LineSegment StartX=-24.1 StartY=39.5 StartZ=0 EndX=-15.1 EndY=39.5 EndZ=0
    g33: LineSegment StartX=-15.1 StartY=39.5 StartZ=0 EndX=-15.5 EndY=34.9 EndZ=0
    g34: LineSegment StartX=-15.5 StartY=34.9 StartZ=0 EndX=-15.1 EndY=32.5 EndZ=0
    g35: LineSegment StartX=-15.1 StartY=32.5 StartZ=0 EndX=-15.5 EndY=27.9 EndZ=0
    g36: LineSegment StartX=-15.5 StartY=27.9 StartZ=0 EndX=-15.1 EndY=25.5 EndZ=0
    g37: LineSegment StartX=-15.1 StartY=25.5 StartZ=0 EndX=-15.5 EndY=20.9 EndZ=0
    g38: LineSegment StartX=-15.5 StartY=20.9 StartZ=0 EndX=-15.1 EndY=18.5 EndZ=0
    g39: LineSegment StartX=-15.1 StartY=18.5 StartZ=0 EndX=-15.5 EndY=13.9 EndZ=0
    g40: LineSegment StartX=-15.5 StartY=13.9 StartZ=0 EndX=-15.1 EndY=11.5 EndZ=0
    g41: LineSegment StartX=-15.1 StartY=11.5 StartZ=0 EndX=-15.1 EndY=4.5 EndZ=0
    g42: LineSegment StartX=-14.3 StartY=4.5 StartZ=0 EndX=-14.3 EndY=11.5 EndZ=0
    g43: LineSegment StartX=-14.3 StartY=11.5 StartZ=0 EndX=-14.7 EndY=13.9 EndZ=0
    g44: LineSegment StartX=-14.7 StartY=13.9 StartZ=0 EndX=-14.3 EndY=18.5 EndZ=0
    g45: LineSegment StartX=-14.3 StartY=18.5 StartZ=0 EndX=-14.7 EndY=20.9 EndZ=0
    g46: LineSegment StartX=-14.7 StartY=20.9 StartZ=0 EndX=-14.3 EndY=25.5 EndZ=0
    g47: LineSegment StartX=-14.3 StartY=25.5 StartZ=0 EndX=-14.7 EndY=27.9 EndZ=0
    g48: LineSegment StartX=-14.7 StartY=27.9 StartZ=0 EndX=-14.3 EndY=32.5 EndZ=0
    g49: LineSegment StartX=-14.3 StartY=32.5 StartZ=0 EndX=-14.7 EndY=34.9 EndZ=0
    g50: LineSegment StartX=-14.7 StartY=34.9 StartZ=0 EndX=-14.3 EndY=39.5 EndZ=0
    g51: LineSegment StartX=-14.3 StartY=39.5 StartZ=0 EndX=-5.3 EndY=39.5 EndZ=0
    g52: LineSegment StartX=-5.3 StartY=39.5 StartZ=0 EndX=-5.7 EndY=34.9 EndZ=0
    g53: LineSegment StartX=-5.7 StartY=34.9 StartZ=0 EndX=-5.3 EndY=32.5 EndZ=0
    g54: LineSegment StartX=-5.3 StartY=32.5 StartZ=0 EndX=-5.7 EndY=27.9 EndZ=0
    g55: LineSegment StartX=-5.7 StartY=27.9 StartZ=0 EndX=-5.3 EndY=25.5 EndZ=0
    g56: LineSegment StartX=-5.3 StartY=25.5 StartZ=0 EndX=-5.7 EndY=20.9 EndZ=0
    g57: LineSegment StartX=-5.7 StartY=20.9 StartZ=0 EndX=-5.3 EndY=18.5 EndZ=0
    g58: LineSegment StartX=-5.3 StartY=18.5 StartZ=0 EndX=-5.7 EndY=13.9 EndZ=0
    g59: LineSegment StartX=-5.7 StartY=13.9 StartZ=0 EndX=-5.3 EndY=11.5 EndZ=0
    g60: LineSegment StartX=-5.3 StartY=11.5 StartZ=0 EndX=-5.3 EndY=4.5 EndZ=0
    g61: LineSegment StartX=-4.5 StartY=4.5 StartZ=0 EndX=-4.5 EndY=11.5 EndZ=0
    g62: LineSegment StartX=-4.5 StartY=11.5 StartZ=0 EndX=-4.9 EndY=13.9 EndZ=0
    g63: LineSegment StartX=-4.9 StartY=13.9 StartZ=0 EndX=-4.5 EndY=18.5 EndZ=0
    g64: LineSegment StartX=-4.5 StartY=18.5 StartZ=0 EndX=-4.9 EndY=20.9 EndZ=0
    g65: LineSegment StartX=-4.9 StartY=20.9 StartZ=0 EndX=-4.5 EndY=25.5 EndZ=0
    g66: LineSegment StartX=-4.5 StartY=25.5 StartZ=0 EndX=-4.9 EndY=27.9 EndZ=0
    g67: LineSegment StartX=-4.9 StartY=27.9 StartZ=0 EndX=-4.5 EndY=32.5 EndZ=0
    g68: LineSegment StartX=-4.5 StartY=32.5 StartZ=0 EndX=-4.9 EndY=34.9 EndZ=0
    g69: LineSegment StartX=-4.9 StartY=34.9 StartZ=0 EndX=-4.5 EndY=39.5 EndZ=0
    g70: LineSegment StartX=-4.5 StartY=39.5 StartZ=0 EndX=4.5 EndY=39.5 EndZ=0
    g71: LineSegment StartX=4.5 StartY=39.5 StartZ=0 EndX=4.9 EndY=34.9 EndZ=0
    g72: LineSegment StartX=4.9 StartY=34.9 StartZ=0 EndX=4.5 EndY=32.5 EndZ=0
    g73: LineSegment StartX=4.5 StartY=32.5 StartZ=0 EndX=4.9 EndY=27.9 EndZ=0
    g74: LineSegment StartX=4.9 StartY=27.9 StartZ=0 EndX=4.5 EndY=25.5 EndZ=0
    g75: LineSegment StartX=4.5 StartY=25.5 StartZ=0 EndX=4.9 EndY=20.9 EndZ=0
    g76: LineSegment StartX=4.9 StartY=20.9 StartZ=0 EndX=4.5 EndY=18.5 EndZ=0
    g77: LineSegment StartX=4.5 StartY=18.5 StartZ=0 EndX=4.9 EndY=13.9 EndZ=0
    g78: LineSegment StartX=4.9 StartY=13.9 StartZ=0 EndX=4.5 EndY=11.5 EndZ=0
    g79: LineSegment StartX=4.5 StartY=11.5 StartZ=0 EndX=4.5 EndY=4.5 EndZ=0
    g80: LineSegment StartX=5.3 StartY=4.5 StartZ=0 EndX=5.3 EndY=11.5 EndZ=0
    g81: LineSegment StartX=5.3 StartY=11.5 StartZ=0 EndX=5.7 EndY=13.9 EndZ=0
    g82: LineSegment StartX=5.7 StartY=13.9 StartZ=0 EndX=5.3 EndY=18.5 EndZ=0
    g83: LineSegment StartX=5.3 StartY=18.5 StartZ=0 EndX=5.7 EndY=20.9 EndZ=0
    g84: LineSegment StartX=5.7 StartY=20.9 StartZ=0 EndX=5.3 EndY=25.5 EndZ=0
    g85: LineSegment StartX=5.3 StartY=25.5 StartZ=0 EndX=5.7 EndY=27.9 EndZ=0
    g86: LineSegment StartX=5.7 StartY=27.9 StartZ=0 EndX=5.3 EndY=32.5 EndZ=0
    g87: LineSegment StartX=5.3 StartY=32.5 StartZ=0 EndX=5.7 EndY=34.9 EndZ=0
    g88: LineSegment StartX=5.7 StartY=34.9 StartZ=0 EndX=5.3 EndY=39.5 EndZ=0
    g89: LineSegment StartX=5.3 StartY=39.5 StartZ=0 EndX=14.3 EndY=39.5 EndZ=0
    g90: LineSegment StartX=14.3 StartY=39.5 StartZ=0 EndX=14.7 EndY=34.9 EndZ=0
    g91: LineSegment StartX=14.7 StartY=34.9 StartZ=0 EndX=14.3 EndY=32.5 EndZ=0
    g92: LineSegment StartX=14.3 StartY=32.5 StartZ=0 EndX=14.7 EndY=27.9 EndZ=0
    g93: LineSegment StartX=14.7 StartY=27.9 StartZ=0 EndX=14.3 EndY=25.5 EndZ=0
    g94: LineSegment StartX=14.3 StartY=25.5 StartZ=0 EndX=14.7 EndY=20.9 EndZ=0
    g95: LineSegment StartX=14.7 StartY=20.9 StartZ=0 EndX=14.3 EndY=18.5 EndZ=0
    g96: LineSegment StartX=14.3 StartY=18.5 StartZ=0 EndX=14.7 EndY=13.9 EndZ=0
    g97: LineSegment StartX=14.7 StartY=13.9 StartZ=0 EndX=14.3 EndY=11.5 EndZ=0
    g98: LineSegment StartX=14.3 StartY=11.5 StartZ=0 EndX=14.3 EndY=4.5 EndZ=0
    g99: LineSegment StartX=15.1 StartY=4.5 StartZ=0 EndX=15.1 EndY=11.5 EndZ=0
    g100: LineSegment StartX=15.1 StartY=11.5 StartZ=0 EndX=15.5 EndY=13.9 EndZ=0
    g101: LineSegment StartX=15.5 StartY=13.9 StartZ=0 EndX=15.1 EndY=18.5 EndZ=0
    g102: LineSegment StartX=15.1 StartY=18.5 StartZ=0 EndX=15.5 EndY=20.9 EndZ=0
    g103: LineSegment StartX=15.5 StartY=20.9 StartZ=0 EndX=15.1 EndY=25.5 EndZ=0
    g104: LineSegment StartX=15.1 StartY=25.5 StartZ=0 EndX=15.5 EndY=27.9 EndZ=0
    g105: LineSegment StartX=15.5 StartY=27.9 StartZ=0 EndX=15.1 EndY=32.5 EndZ=0
    g106: LineSegment StartX=15.1 StartY=32.5 StartZ=0 EndX=15.5 EndY=34.9 EndZ=0
    g107: LineSegment StartX=15.5 StartY=34.9 StartZ=0 EndX=15.1 EndY=39.5 EndZ=0
    g108: LineSegment StartX=15.1 StartY=39.5 StartZ=0 EndX=24.1 EndY=39.5 EndZ=0
    g109: LineSegment StartX=24.1 StartY=39.5 StartZ=0 EndX=24.5 EndY=34.9 EndZ=0
    g110: LineSegment StartX=24.5 StartY=34.9 StartZ=0 EndX=24.1 EndY=32.5 EndZ=0
    g111: LineSegment StartX=24.1 StartY=32.5 StartZ=0 EndX=24.5 EndY=27.9 EndZ=0
    g112: LineSegment StartX=24.5 StartY=27.9 StartZ=0 EndX=24.1 EndY=25.5 EndZ=0
    g113: LineSegment StartX=24.1 StartY=25.5 StartZ=0 EndX=24.5 EndY=20.9 EndZ=0
    g114: LineSegment StartX=24.5 StartY=20.9 StartZ=0 EndX=24.1 EndY=18.5 EndZ=0
    g115: LineSegment StartX=24.1 StartY=18.5 StartZ=0 EndX=24.5 EndY=13.9 EndZ=0
    g116: LineSegment StartX=24.5 StartY=13.9 StartZ=0 EndX=24.1 EndY=11.5 EndZ=0
    g117: LineSegment StartX=24.1 StartY=11.5 StartZ=0 EndX=24.1 EndY=4.5 EndZ=0
    g118: LineSegment StartX=24.9 StartY=4.5 StartZ=0 EndX=24.9 EndY=11.5 EndZ=0
    g119: LineSegment StartX=24.9 StartY=11.5 StartZ=0 EndX=25.3 EndY=13.9 EndZ=0
    g120: LineSegment StartX=25.3 StartY=13.9 StartZ=0 EndX=24.9 EndY=18.5 EndZ=0
    g121: LineSegment StartX=24.9 StartY=18.5 StartZ=0 EndX=25.3 EndY=20.9 EndZ=0
    g122: LineSegment StartX=25.3 StartY=20.9 StartZ=0 EndX=24.9 EndY=25.5 EndZ=0
    g123: LineSegment StartX=24.9 StartY=25.5 StartZ=0 EndX=25.3 EndY=27.9 EndZ=0
    g124: LineSegment StartX=25.3 StartY=27.9 StartZ=0 EndX=24.9 EndY=32.5 EndZ=0
    g125: LineSegment StartX=24.9 StartY=32.5 StartZ=0 EndX=25.3 EndY=34.9 EndZ=0
    g126: LineSegment StartX=25.3 StartY=34.9 StartZ=0 EndX=24.9 EndY=39.5 EndZ=0
    g127: LineSegment StartX=24.9 StartY=39.5 StartZ=0 EndX=33.9 EndY=39.5 EndZ=0
    g128: LineSegment StartX=33.9 StartY=39.5 StartZ=0 EndX=34.3 EndY=34.9 EndZ=0
    g129: LineSegment StartX=34.3 StartY=34.9 StartZ=0 EndX=33.9 EndY=32.5 EndZ=0
    g130: LineSegment StartX=33.9 StartY=32.5 StartZ=0 EndX=34.3 EndY=27.9 EndZ=0
    g131: LineSegment StartX=34.3 StartY=27.9 StartZ=0 EndX=33.9 EndY=25.5 EndZ=0
    g132: LineSegment StartX=33.9 StartY=25.5 StartZ=0 EndX=34.3 EndY=20.9 EndZ=0
    g133: LineSegment StartX=34.3 StartY=20.9 StartZ=0 EndX=33.9 EndY=18.5 EndZ=0
    g134: LineSegment StartX=33.9 StartY=18.5 StartZ=0 EndX=34.3 EndY=13.9 EndZ=0
    g135: LineSegment StartX=34.3 StartY=13.9 StartZ=0 EndX=33.9 EndY=11.5 EndZ=0
    g136: LineSegment StartX=33.9 StartY=11.5 StartZ=0 EndX=33.9 EndY=0 EndZ=0
    g137: LineSegment StartX=33.9 StartY=0 StartZ=0 EndX=-33.9 EndY=0 EndZ=0
    g138: LineSegment StartX=-73.1099 StartY=18.5 StartZ=0 EndX=65.6354 EndY=18.5 EndZ=0
    g139: LineSegment StartX=-73.1099 StartY=34.9 StartZ=0 EndX=65.6354 EndY=34.9 EndZ=0
    g140: LineSegment StartX=-73.1099 StartY=32.5 StartZ=0 EndX=65.6354 EndY=32.5 EndZ=0
    g141: LineSegment StartX=-73.1099 StartY=27.9 StartZ=0 EndX=65.6354 EndY=27.9 EndZ=0
    g142: LineSegment StartX=-73.1099 StartY=20.9 StartZ=0 EndX=65.6354 EndY=20.9 EndZ=0
    g143: LineSegment StartX=-73.1099 StartY=11.5 StartZ=0 EndX=65.6354 EndY=11.5 EndZ=0
    g144: LineSegment StartX=-34.3 StartY=8.59208 StartZ=0 EndX=-34.3 EndY=49.4346 EndZ=0
    g145: LineSegment StartX=-73.1099 StartY=13.9 StartZ=0 EndX=65.6354 EndY=13.9 EndZ=0
    g146: LineSegment StartX=-33.9 StartY=0 StartZ=0 EndX=33.9 EndY=0 EndZ=0
    g147: LineSegment StartX=-73.1099 StartY=4.5 StartZ=0 EndX=65.6354 EndY=4.5 EndZ=0
    g148: ArcOfCircle CenterX=-24.5 CenterY=3 CenterZ=0 NormalX=0 NormalY=0 NormalZ=1 AngleXU=0 Radius=1.55242 StartAngle=1.8314 EndAngle=7.59338
    g149: ArcOfCircle CenterX=-14.7 CenterY=3 CenterZ=0 NormalX=0 NormalY=0 NormalZ=1 AngleXU=0 Radius=1.55242 StartAngle=1.8314 EndAngle=7.59338
    g150: ArcOfCircle CenterX=-4.9 CenterY=3 CenterZ=0 NormalX=0 NormalY=0 NormalZ=1 AngleXU=0 Radius=1.55242 StartAngle=1.8314 EndAngle=7.59338
    g151: ArcOfCircle CenterX=4.9 CenterY=3 CenterZ=0 NormalX=0 NormalY=0 NormalZ=1 AngleXU=0 Radius=1.55242 StartAngle=1.8314 EndAngle=7.59338
    g152: ArcOfCircle CenterX=14.7 CenterY=3 CenterZ=0 NormalX=0 NormalY=0 NormalZ=1 AngleXU=0 Radius=1.55242 StartAngle=1.8314 EndAngle=7.59338
    g153: ArcOfCircle CenterX=24.5 CenterY=3 CenterZ=0 NormalX=0 NormalY=0 NormalZ=1 AngleXU=0 Radius=1.55242 StartAngle=1.8314 EndAngle=7.59338
    g154: LineSegment StartX=-73.1099 StartY=3 StartZ=0 EndX=65.6354 EndY=3 EndZ=0
  constraints (469):
    c: Coincident(g0,g1)
    c: Coincident(g1,g2)
    c: Horizontal(g3)
    c: Symmetric(g0,g2,g-2)
    c: Symmetric(g1,g0,g-2)
    c: DistanceX(g0,g2) = 67.8
    c: DistanceX(g0,g1) = 67.8
    c: Coincident(g4,g5)
    c: Coincident(g5,g6)
    c: Coincident(g6,g7)
    c: Coincident(g7,g8)
    c: Coincident(g8,g9)
    c: Coincident(g9,g10)
    c: Coincident(g10,g11)
    c: Coincident(g11,g12)
    c: Coincident(g12,g13)
    c: Horizontal(g13)
    c: Coincident(g13,g14)
    c: Coincident(g14,g15)
    c: Coincident(g15,g16)
    c: Coincident(g16,g17)
    c: Coincident(g17,g18)
    c: Coincident(g18,g19)
    c: Coincident(g19,g20)
    c: Coincident(g20,g21)
    c: Coincident(g21,g22)
    c: Coincident(g23,g24)
    c: Coincident(g24,g25)
    c: Coincident(g25,g26)
    c: Coincident(g26,g27)
    c: Coincident(g27,g28)
    c: Coincident(g28,g29)
    c: Coincident(g29,g30)
    c: Coincident(g30,g31)
    c: Coincident(g31,g32)
    c: Horizontal(g32)
    c: Coincident(g32,g33)
    c: Coincident(g33,g34)
    c: Coincident(g34,g35)
    c: Coincident(g35,g36)
    c: Coincident(g36,g37)
    c: Coincident(g37,g38)
    c: Coincident(g38,g39)
    c: Coincident(g39,g40)
    c: Coincident(g40,g41)
    c: Coincident(g42,g43)
    c: Coincident(g43,g44)
    c: Coincident(g44,g45)
    c: Coincident(g45,g46)
    c: Coincident(g46,g47)
    c: Coincident(g47,g48)
    c: Coincident(g48,g49)
    c: Coincident(g49,g50)
    c: Coincident(g50,g51)
    c: Coincident(g51,g52)
    c: Coincident(g52,g53)
    c: Coincident(g53,g54)
    c: Coincident(g54,g55)
    c: Coincident(g55,g56)
    c: Coincident(g56,g57)
    c: Coincident(g57,g58)
    c: Coincident(g58,g59)
    c: Coincident(g59,g60)
    c: Coincident(g61,g62)
    c: Coincident(g62,g63)
    c: Coincident(g63,g64)
    c: Coincident(g64,g65)
    c: Coincident(g65,g66)
    c: Coincident(g66,g67)
    c: Coincident(g67,g68)
    c: Coincident(g68,g69)
    c: Coincident(g69,g70)
    c: Coincident(g70,g71)
    c: Coincident(g71,g72)
    c: Coincident(g72,g73)
    c: Coincident(g73,g74)
    c: Coincident(g74,g75)
    c: Coincident(g75,g76)
    c: Coincident(g76,g77)
    c: Coincident(g77,g78)
    c: Coincident(g78,g79)
    c: Coincident(g80,g81)
    c: Coincident(g81,g82)
    c: Coincident(g82,g83)
    c: Coincident(g83,g84)
    c: Coincident(g84,g85)
    c: Coincident(g85,g86)
    c: Coincident(g86,g87)
    c: Coincident(g87,g88)
    c: Coincident(g88,g89)
    c: Horizontal(g89)
    c: Coincident(g89,g90)
    c: Coincident(g90,g91)
    c: Coincident(g91,g92)
    c: Coincident(g92,g93)
    c: Coincident(g93,g94)
    c: Coincident(g94,g95)
    c: Coincident(g95,g96)
    c: Coincident(g96,g97)
    c: Coincident(g97,g98)
    c: Coincident(g99,g100)
    c: Coincident(g100,g101)
    c: Coincident(g101,g102)
    c: Coincident(g102,g103)
    c: Coincident(g103,g104)
    c: Coincident(g104,g105)
    c: Coincident(g105,g106)
    c: Coincident(g106,g107)
    c: Coincident(g107,g108)
    c: Coincident(g108,g109)
    c: Coincident(g109,g110)
    c: Coincident(g110,g111)
    c: Coincident(g111,g112)
    c: Coincident(g112,g113)
    c: Coincident(g113,g114)
    c: Coincident(g114,g115)
    c: Coincident(g115,g116)
    c: Coincident(g116,g117)
    c: Coincident(g118,g119)
    c: Coincident(g119,g120)
    c: Coincident(g120,g121)
    c: Coincident(g121,g122)
    c: Coincident(g122,g123)
    c: Coincident(g123,g124)
    c: Coincident(g124,g125)
    c: Coincident(g125,g126)
    c: Coincident(g126,g127)
    c: Coincident(g127,g128)
    c: Coincident(g128,g129)
    c: Coincident(g129,g130)
    c: Coincident(g130,g131)
    c: Coincident(g131,g132)
    c: Coincident(g132,g133)
    c: Coincident(g133,g134)
    c: Coincident(g134,g135)
    c: Coincident(g135,g136)
    c: Symmetric(g69,g70,g-2)
    c: Symmetric(g51,g88,g-2)
    c: Symmetric(g50,g89,g-2)
    c: Symmetric(g32,g107,g-2)
    c: Symmetric(g31,g108,g-2)
    c: Symmetric(g13,g126,g-2)
    c: Symmetric(g12,g127,g-2)
    c: DistanceX(g13,g31) = 0.8
    c: DistanceX(g32,g50) = 0.8
    c: DistanceX(g51,g69) = 0.8
    c: DistanceX(g13,g13) = 9
    c: DistanceX(g32,g32) = 9
    c: DistanceX(g51,g51) = 9
    c: Horizontal(g139)
    c: Horizontal(g140)
    c: Horizontal(g141)
    c: Horizontal(g142)
    c: Horizontal(g143)
    c: Vertical(g8,g6)
    c: Vertical(g6,g4)
    c: Vertical(g144)
    c: Horizontal(g145)
    c: Coincident(g146,g0)
    c: Coincident(g146,g2)
    c: Coincident(g0,g137)
    c: Coincident(g2,g137)
    c: Horizontal(g147)
    c: PointOnObject(g11,g139)
    c: PointOnObject(g11,g144)
    c: PointOnObject(g10,g140)
    c: PointOnObject(g9,g144)
    c: PointOnObject(g7,g142)
    c: Horizontal(g138)
    c: DistanceY(g137,g147) = 4.5
    c: DistanceY(g147,g143) = 7
    c: DistanceY(g143,g138) = 7
    c: DistanceY(g138,g3) = 7
    c: DistanceY(g3,g140) = 7
    c: DistanceY(g140,g0) = 7
    c: Vertical(g139,g140)
    c: Vertical(g140,g141)
    c: Vertical(g141,g3)
    c: Vertical(g3,g142)
    c: Vertical(g142,g138)
    c: Vertical(g138,g145)
    c: Vertical(g145,g143)
    c: Vertical(g143,g147)
    c: DistanceY(g143,g145) = 2.4
    c: DistanceY(g138,g142) = 2.4
    c: DistanceY(g3,g141) = 2.4
    c: DistanceY(g140,g139) = 2.4
    c: Parallel(g12,g14)
    c: Parallel(g11,g15)
    c: PointOnObject(g14,g139)
    c: PointOnObject(g30,g139)
    c: PointOnObject(g15,g140)
    c: PointOnObject(g29,g140)
    c: Parallel(g14,g31)
    c: PointOnObject(g16,g141)
    c: PointOnObject(g28,g141)
    c: PointOnObject(g17,g3)
    c: PointOnObject(g27,g3)
    c: PointOnObject(g18,g142)
    c: PointOnObject(g26,g142)
    c: PointOnObject(g19,g138)
    c: PointOnObject(g25,g138)
    c: PointOnObject(g20,g145)
    c: PointOnObject(g24,g145)
    c: PointOnObject(g21,g143)
    c: PointOnObject(g23,g143)
    c: PointOnObject(g22,g147)
    c: PointOnObject(g23,g147)
    c: PointOnObject(g33,g139)
    c: PointOnObject(g49,g139)
    c: PointOnObject(g52,g139)
    c: PointOnObject(g71,g139)
    c: PointOnObject(g87,g139)
    c: PointOnObject(g90,g139)
    c: PointOnObject(g106,g139)
    c: PointOnObject(g109,g139)
    c: PointOnObject(g125,g139)
    c: PointOnObject(g128,g139)
    c: PointOnObject(g34,g140)
    c: PointOnObject(g48,g140)
    c: PointOnObject(g53,g140)
    c: PointOnObject(g67,g140)
    c: PointOnObject(g72,g140)
    c: PointOnObject(g86,g140)
    c: PointOnObject(g91,g140)
    c: PointOnObject(g105,g140)
    c: PointOnObject(g110,g140)
    c: PointOnObject(g124,g140)
    c: PointOnObject(g129,g140)
    c: Parallel(g33,g50)
    c: Parallel(g52,g69)
    c: Parallel(g71,g88)
    c: Parallel(g71,g90)
    c: Parallel(g90,g107)
    c: Parallel(g71,g109)
    c: Parallel(g109,g126)
    c: Parallel(g126,g128)
    c: Symmetric(g71,g68,g-2)
    c: Symmetric(g72,g67,g-2)
    c: Vertical(g139,g140)
    c: Vertical(g140,g141)
    c: Vertical(g141,g3)
    c: Vertical(g3,g142)
    c: Vertical(g142,g138)
    c: Vertical(g138,g145)
    c: Vertical(g145,g143)
    c: Vertical(g143,g147)
    c: Parallel(g34,g49)
    c: Parallel(g49,g53)
    c: Parallel(g53,g68)
    c: Parallel(g35,g48)
    c: Parallel(g48,g54)
    c: Parallel(g54,g67)
    c: PointOnObject(g35,g141)
    c: PointOnObject(g47,g141)
    c: PointOnObject(g54,g141)
    c: PointOnObject(g66,g141)
    c: PointOnObject(g85,g141)
    c: PointOnObject(g92,g141)
    c: PointOnObject(g104,g141)
    c: PointOnObject(g111,g141)
    c: PointOnObject(g123,g141)
    c: PointOnObject(g130,g141)
    c: Symmetric(g66,g73,g-2)
    c: Symmetric(g65,g74,g-2)
    c: PointOnObject(g36,g3)
    c: PointOnObject(g46,g3)
    c: PointOnObject(g55,g3)
    c: PointOnObject(g65,g3)
    c: Parallel(g36,g47)
    c: Parallel(g47,g55)
    c: Parallel(g55,g66)
    c: Symmetric(g64,g75,g-2)
    c: Symmetric(g79,g61,g-2)
    c: Symmetric(g61,g78,g-2)
    c: Symmetric(g62,g77,g-2)
    c: Symmetric(g63,g76,g-2)
    c: Parallel(g37,g46)
    c: Parallel(g46,g56)
    c: Parallel(g56,g65)
    c: PointOnObject(g37,g142)
    c: PointOnObject(g45,g142)
    c: PointOnObject(g56,g142)
    c: PointOnObject(g64,g142)
    c: PointOnObject(g38,g138)
    c: PointOnObject(g44,g138)
    c: PointOnObject(g57,g138)
    c: PointOnObject(g63,g138)
    c: Parallel(g38,g45)
    c: Parallel(g45,g57)
    c: Parallel(g57,g64)
    c: PointOnObject(g39,g145)
    c: PointOnObject(g43,g145)
    c: PointOnObject(g58,g145)
    c: PointOnObject(g62,g145)
    c: Parallel(g39,g44)
    c: Parallel(g44,g58)
    c: Parallel(g58,g63)
    c: Parallel(g40,g43)
    c: Parallel(g43,g59)
    c: Parallel(g59,g62)
    c: PointOnObject(g40,g143)
    c: PointOnObject(g42,g143)
    c: PointOnObject(g59,g143)
    c: PointOnObject(g61,g143)
    c: PointOnObject(g41,g147)
    c: PointOnObject(g42,g147)
    c: PointOnObject(g60,g147)
    c: PointOnObject(g61,g147)
    c: Parallel(g41,g42)
    c: Parallel(g42,g60)
    c: Parallel(g60,g61)
    c: PointOnObject(g80,g147)
    c: PointOnObject(g98,g147)
    c: PointOnObject(g99,g147)
    c: PointOnObject(g117,g147)
    c: PointOnObject(g118,g147)
    c: PointOnObject(g80,g143)
    c: PointOnObject(g97,g143)
    c: PointOnObject(g99,g143)
    c: PointOnObject(g116,g143)
    c: PointOnObject(g118,g143)
    c: PointOnObject(g135,g143)
    c: Parallel(g79,g80)
    c: Parallel(g80,g98)
    c: Parallel(g98,g99)
    c: Parallel(g99,g117)
    c: Parallel(g117,g118)
    c: Parallel(g118,g136)
    c: Parallel(g72,g87)
    c: Parallel(g87,g91)
    c: Parallel(g91,g106)
    c: Parallel(g106,g110)
    c: Parallel(g110,g125)
    c: Parallel(g125,g129)
    c: Parallel(g73,g86)
    c: Parallel(g86,g92)
    c: Parallel(g92,g105)
    c: Parallel(g105,g111)
    c: Parallel(g111,g124)
    c: Parallel(g124,g130)
    c: PointOnObject(g84,g3)
    c: PointOnObject(g93,g3)
    c: PointOnObject(g103,g3)
    c: PointOnObject(g112,g3)
    c: PointOnObject(g122,g3)
    c: PointOnObject(g131,g3)
    c: Parallel(g74,g85)
    c: Parallel(g85,g93)
    c: Parallel(g93,g104)
    c: Parallel(g104,g112)
    c: Parallel(g112,g123)
    c: Parallel(g123,g131)
    c: PointOnObject(g83,g142)
    c: PointOnObject(g94,g142)
    c: PointOnObject(g102,g142)
    c: PointOnObject(g113,g142)
    c: PointOnObject(g121,g142)
    c: PointOnObject(g132,g142)
    c: Parallel(g75,g84)
    c: Parallel(g84,g94)
    c: Parallel(g94,g103)
    c: Parallel(g103,g113)
    c: Parallel(g113,g122)
    c: Parallel(g122,g132)
    c: PointOnObject(g82,g138)
    c: PointOnObject(g95,g138)
    c: PointOnObject(g101,g138)
    c: PointOnObject(g114,g138)
    c: PointOnObject(g120,g138)
    c: PointOnObject(g133,g138)
    c: PointOnObject(g81,g145)
    c: PointOnObject(g96,g145)
    c: PointOnObject(g100,g145)
    c: PointOnObject(g115,g145)
    c: PointOnObject(g119,g145)
    c: PointOnObject(g134,g145)
    c: Parallel(g76,g83)
    c: Parallel(g83,g95)
    c: Parallel(g95,g102)
    c: Parallel(g102,g114)
    c: Parallel(g114,g121)
    c: Parallel(g121,g133)
    c: Parallel(g77,g82)
    c: Parallel(g82,g96)
    c: Parallel(g96,g101)
    c: Parallel(g101,g115)
    c: Parallel(g115,g120)
    c: Parallel(g120,g134)
    c: Parallel(g78,g81)
    c: Parallel(g81,g97)
    c: Parallel(g97,g100)
    c: Parallel(g100,g116)
    c: Parallel(g116,g119)
    c: Parallel(g119,g135)
    c: DistanceY(g137,g-1) = 0
    c: PointOnObject(g148,g154)
    c: PointOnObject(g149,g154)
    c: PointOnObject(g150,g154)
    c: PointOnObject(g151,g154)
    c: PointOnObject(g152,g154)
    c: PointOnObject(g153,g154)
    c: PointOnObject(g22,g148)
    c: PointOnObject(g23,g148)
    c: PointOnObject(g41,g149)
    c: PointOnObject(g42,g149)
    c: PointOnObject(g60,g150)
    c: PointOnObject(g61,g150)
    c: PointOnObject(g79,g151)
    c: PointOnObject(g98,g152)
    c: PointOnObject(g99,g152)
    c: PointOnObject(g117,g153)
    c: PointOnObject(g118,g153)
    c: PointOnObject(g153,g147)
    c: PointOnObject(g153,g147)
    c: PointOnObject(g152,g147)
    c: PointOnObject(g152,g147)
    c: PointOnObject(g151,g147)
    c: PointOnObject(g151,g147)
    c: PointOnObject(g150,g147)
    c: PointOnObject(g150,g147)
    c: PointOnObject(g149,g147)
    c: PointOnObject(g149,g147)
    c: PointOnObject(g148,g147)
    c: PointOnObject(g148,g147)
    c: DistanceY(g154,g147) = 1.5
    c: Vertical(g147,g154)
    c: Vertical(g147,g154)
    c: Coincident(g136,g137)
    c: Coincident(g4,g137)
    c: Coincident(g0,g12)
    c: PointOnObject(g31,g1)
    c: PointOnObject(g50,g1)
    c: PointOnObject(g69,g1)
    c: PointOnObject(g6,g0)
    c: DistanceX(g144,g12) = 0.4
    c: PointOnObject(g9,g141)
    c: PointOnObject(g8,g3)
    c: PointOnObject(g7,g144)
    c: PointOnObject(g6,g138)
    c: PointOnObject(g5,g145)
    c: PointOnObject(g5,g144)
    c: PointOnObject(g4,g143)
    c: Parallel(g12,g33)
    c: Parallel(g12,g52)
    c: Parallel(g15,g30)
    c: Parallel(g11,g34)
    c: PointOnObject(g10,g0)
    c: Parallel(g16,g29)
    c: Parallel(g10,g16)
    c: Parallel(g10,g35)
    c: Parallel(g9,g17)
    c: Parallel(g17,g28)
    c: Parallel(g9,g36)
    c: Parallel(g18,g27)
    c: Parallel(g8,g18)
    c: Parallel(g8,g37)
    c: Parallel(g7,g19)
    c: Parallel(g19,g26)
    c: Parallel(g6,g20)
    c: Parallel(g20,g25)
    c: Parallel(g7,g38)
    c: Parallel(g6,g39)
    c: Symmetric(g150,g151,g-2)
    c: DistanceX(g150,g151) = 9.8
    c: Parallel(g23,g22)
    c: Parallel(g21,g24)
    c: Parallel(g5,g21)
    c: Parallel(g41,g23)
FEATURE [PartDesign::Pad] Pad  label="FixatorPadBody"
  Direction = (0,0,1)
  Length = 6
  Length2 = 10
  Profile = -> Sketch022
  ReferenceAxis = -> Sketch022 [N_Axis]
  Type = 0
  expr: Length = Spreadsheet.mmCellHight
FEATURE [Sketcher::SketchObject] Sketch  label="PiercesPocketSketch"
  AttachmentOffset = pos=(0,0,0) rot=(1,0,0;1.5708rad)
  FullyConstrained = true
  MapMode = 2
  Placement = pos=(0,0,0) rot=(0.707107,0.707107,0;3.14159rad)
  Support = -> [YZ_Plane005]
  expr: Constraints[108] = Spreadsheet.mmCellPierceWidth
  expr: Constraints[118] = Spreadsheet.mmCellPierceWidth
  expr: Constraints[128] = Spreadsheet.mmCellPierceWidth
  expr: Constraints[138] = Spreadsheet.mmCellPierceWidth
  expr: Constraints[148] = Spreadsheet.mmCellPierceWidth
  expr: Constraints[158] = Spreadsheet.mmCellPierceWidth
  expr: Constraints[171] = Spreadsheet.mmCellWidth + Spreadsheet.mmCellWall
  expr: Constraints[172] = Spreadsheet.mmCellWidth + Spreadsheet.mmCellWall
  expr: Constraints[173] = Spreadsheet.mmCellWidth + Spreadsheet.mmCellWall
  expr: Constraints[174] = Spreadsheet.mmCellWidth + Spreadsheet.mmCellWall
  expr: Constraints[175] = Spreadsheet.mmCellWidth + Spreadsheet.mmCellWall
  expr: Constraints[176] = Spreadsheet.mmCellWidth + Spreadsheet.mmCellWall
  expr: Constraints[178] = Spreadsheet.mmCellWidth / 2
  expr: Constraints[179] = Spreadsheet.mmCellWidth / 2
  expr: Constraints[180] = Spreadsheet.mmCommonBaseLenght + Spreadsheet.mmToothStep * 1.5
  expr: Constraints[181] = Spreadsheet.mmToothStep * 2
  expr: Constraints[19] = Spreadsheet.mmCellPierceWidth
  expr: Constraints[29] = Spreadsheet.mmCellPierceWidth
  expr: Constraints[39] = Spreadsheet.mmCellPierceWidth
  expr: Constraints[49] = Spreadsheet.mmCellPierceWidth
  expr: Constraints[59] = Spreadsheet.mmCellPierceWidth
  expr: Constraints[69] = Spreadsheet.mmCellPierceWidth
  expr: Constraints[82] = Spreadsheet.mmCellWidth + Spreadsheet.mmCellWall
  expr: Constraints[83] = Spreadsheet.mmCellWidth + Spreadsheet.mmCellWall
  expr: Constraints[84] = Spreadsheet.mmCellWidth + Spreadsheet.mmCellWall
  expr: Constraints[85] = Spreadsheet.mmCellWidth + Spreadsheet.mmCellWall
  expr: Constraints[86] = Spreadsheet.mmCellWidth + Spreadsheet.mmCellWall
  expr: Constraints[87] = Spreadsheet.mmCellWidth + Spreadsheet.mmCellWall
  expr: Constraints[98] = Spreadsheet.mmCellPierceWidth
  expr: Constraints[9] = Spreadsheet.mmCellPierceWidth
  sketch-geometry (56):
    g0: ArcOfCircle CenterX=29 CenterY=0 CenterZ=0 NormalX=0 NormalY=0 NormalZ=1 AngleXU=0 Radius=3.0104 StartAngle=2.41495 EndAngle=3.86823
    g1: LineSegment StartX=26.75 StartY=2 StartZ=0 EndX=31.25 EndY=2 EndZ=0
    g2: LineSegment StartX=26.75 StartY=-2 StartZ=0 EndX=31.25 EndY=-2 EndZ=0
    g3: ArcOfCircle CenterX=29 CenterY=0 CenterZ=0 NormalX=0 NormalY=0 NormalZ=1 AngleXU=0 Radius=3.0104 StartAngle=5.55654 EndAngle=7.00983
    g4: ArcOfCircle CenterX=29 CenterY=9.8 CenterZ=0 NormalX=0 NormalY=0 NormalZ=1 AngleXU=0 Radius=3.0104 StartAngle=2.41495 EndAngle=3.86823
    g5: LineSegment StartX=26.75 StartY=11.8 StartZ=0 EndX=31.25 EndY=11.8 EndZ=0
    g6: LineSegment StartX=26.75 StartY=7.8 StartZ=0 EndX=31.25 EndY=7.8 EndZ=0
    g7: ArcOfCircle CenterX=29 CenterY=9.8 CenterZ=0 NormalX=0 NormalY=0 NormalZ=1 AngleXU=0 Radius=3.0104 StartAngle=5.55654 EndAngle=7.00983
    g8: ArcOfCircle CenterX=29 CenterY=19.6 CenterZ=0 NormalX=0 NormalY=0 NormalZ=1 AngleXU=0 Radius=3.0104 StartAngle=2.41495 EndAngle=3.86823
    g9: LineSegment StartX=26.75 StartY=21.6 StartZ=0 EndX=31.25 EndY=21.6 EndZ=0
    g10: LineSegment StartX=26.75 StartY=17.6 StartZ=0 EndX=31.25 EndY=17.6 EndZ=0
    g11: ArcOfCircle CenterX=29 CenterY=19.6 CenterZ=0 NormalX=0 NormalY=0 NormalZ=1 AngleXU=0 Radius=3.0104 StartAngle=5.55654 EndAngle=7.00983
    g12: ArcOfCircle CenterX=29 CenterY=29.4 CenterZ=0 NormalX=0 NormalY=0 NormalZ=1 AngleXU=0 Radius=3.0104 StartAngle=2.41495 EndAngle=3.86823
    g13: LineSegment StartX=26.75 StartY=31.4 StartZ=0 EndX=31.25 EndY=31.4 EndZ=0
    g14: LineSegment StartX=26.75 StartY=27.4 StartZ=0 EndX=31.25 EndY=27.4 EndZ=0
    g15: ArcOfCircle CenterX=29 CenterY=29.4 CenterZ=0 NormalX=0 NormalY=0 NormalZ=1 AngleXU=0 Radius=3.0104 StartAngle=5.55654 EndAngle=7.00983
    g16: ArcOfCircle CenterX=29 CenterY=-9.8 CenterZ=0 NormalX=0 NormalY=0 NormalZ=1 AngleXU=0 Radius=3.0104 StartAngle=2.41495 EndAngle=3.86823
    g17: LineSegment StartX=26.75 StartY=-7.8 StartZ=0 EndX=31.25 EndY=-7.8 EndZ=0
    g18: LineSegment StartX=26.75 StartY=-11.8 StartZ=0 EndX=31.25 EndY=-11.8 EndZ=0
    g19: ArcOfCircle CenterX=29 CenterY=-9.8 CenterZ=0 NormalX=0 NormalY=0 NormalZ=1 AngleXU=0 Radius=3.0104 StartAngle=5.55654 EndAngle=7.00983
    g20: ArcOfCircle CenterX=29 CenterY=-19.6 CenterZ=0 NormalX=0 NormalY=0 NormalZ=1 AngleXU=0 Radius=3.0104 StartAngle=2.41495 EndAngle=3.86823
    g21: LineSegment StartX=26.75 StartY=-17.6 StartZ=0 EndX=31.25 EndY=-17.6 EndZ=0
    g22: LineSegment StartX=26.75 StartY=-21.6 StartZ=0 EndX=31.25 EndY=-21.6 EndZ=0
    g23: ArcOfCircle CenterX=29 CenterY=-19.6 CenterZ=0 NormalX=0 NormalY=0 NormalZ=1 AngleXU=0 Radius=3.0104 StartAngle=5.55654 EndAngle=7.00983
    g24: ArcOfCircle CenterX=29 CenterY=-29.4 CenterZ=0 NormalX=0 NormalY=0 NormalZ=1 AngleXU=0 Radius=3.0104 StartAngle=2.41495 EndAngle=3.86823
    g25: LineSegment StartX=26.75 StartY=-27.4 StartZ=0 EndX=31.25 EndY=-27.4 EndZ=0
    g26: LineSegment StartX=26.75 StartY=-31.4 StartZ=0 EndX=31.25 EndY=-31.4 EndZ=0
    g27: ArcOfCircle CenterX=29 CenterY=-29.4 CenterZ=0 NormalX=0 NormalY=0 NormalZ=1 AngleXU=0 Radius=3.0104 StartAngle=5.55654 EndAngle=7.00983
    g28: ArcOfCircle CenterX=15 CenterY=0 CenterZ=0 NormalX=0 NormalY=0 NormalZ=1 AngleXU=0 Radius=3.0104 StartAngle=2.41495 EndAngle=3.86823
    g29: LineSegment StartX=12.75 StartY=2 StartZ=0 EndX=17.25 EndY=2 EndZ=0
    g30: LineSegment StartX=12.75 StartY=-2 StartZ=0 EndX=17.25 EndY=-2 EndZ=0
    g31: ArcOfCircle CenterX=15 CenterY=0 CenterZ=0 NormalX=0 NormalY=0 NormalZ=1 AngleXU=0 Radius=3.0104 StartAngle=5.55654 EndAngle=7.00983
    g32: ArcOfCircle CenterX=15 CenterY=9.8 CenterZ=0 NormalX=0 NormalY=0 NormalZ=1 AngleXU=0 Radius=3.0104 StartAngle=2.41495 EndAngle=3.86823
    g33: LineSegment StartX=12.75 StartY=11.8 StartZ=0 EndX=17.25 EndY=11.8 EndZ=0
    g34: LineSegment StartX=12.75 StartY=7.8 StartZ=0 EndX=17.25 EndY=7.8 EndZ=0
    g35: ArcOfCircle CenterX=15 CenterY=9.8 CenterZ=0 NormalX=0 NormalY=0 NormalZ=1 AngleXU=0 Radius=3.0104 StartAngle=5.55654 EndAngle=7.00983
    g36: ArcOfCircle CenterX=15 CenterY=19.6 CenterZ=0 NormalX=0 NormalY=0 NormalZ=1 AngleXU=0 Radius=3.0104 StartAngle=2.41495 EndAngle=3.86823
    g37: LineSegment StartX=12.75 StartY=21.6 StartZ=0 EndX=17.25 EndY=21.6 EndZ=0
    g38: LineSegment StartX=12.75 StartY=17.6 StartZ=0 EndX=17.25 EndY=17.6 EndZ=0
    g39: ArcOfCircle CenterX=15 CenterY=19.6 CenterZ=0 NormalX=0 NormalY=0 NormalZ=1 AngleXU=0 Radius=3.0104 StartAngle=5.55654 EndAngle=7.00983
    g40: ArcOfCircle CenterX=15 CenterY=29.4 CenterZ=0 NormalX=0 NormalY=0 NormalZ=1 AngleXU=0 Radius=3.0104 StartAngle=2.41495 EndAngle=3.86823
    g41: LineSegment StartX=12.75 StartY=31.4 StartZ=0 EndX=17.25 EndY=31.4 EndZ=0
    g42: LineSegment StartX=12.75 StartY=27.4 StartZ=0 EndX=17.25 EndY=27.4 EndZ=0
    g43: ArcOfCircle CenterX=15 CenterY=29.4 CenterZ=0 NormalX=0 NormalY=0 NormalZ=1 AngleXU=0 Radius=3.0104 StartAngle=5.55654 EndAngle=7.00983
    g44: ArcOfCircle CenterX=15 CenterY=-9.8 CenterZ=0 NormalX=0 NormalY=0 NormalZ=1 AngleXU=0 Radius=3.0104 StartAngle=2.41495 EndAngle=3.86823
    g45: LineSegment StartX=12.75 StartY=-7.8 StartZ=0 EndX=17.25 EndY=-7.8 EndZ=0
    g46: LineSegment StartX=12.75 StartY=-11.8 StartZ=0 EndX=17.25 EndY=-11.8 EndZ=0
    g47: ArcOfCircle CenterX=15 CenterY=-9.8 CenterZ=0 NormalX=0 NormalY=0 NormalZ=1 AngleXU=0 Radius=3.0104 StartAngle=5.55654 EndAngle=7.00983
    g48: ArcOfCircle CenterX=15 CenterY=-19.6 CenterZ=0 NormalX=0 NormalY=0 NormalZ=1 AngleXU=0 Radius=3.0104 StartAngle=2.41495 EndAngle=3.86823
    g49: LineSegment StartX=12.75 StartY=-17.6 StartZ=0 EndX=17.25 EndY=-17.6 EndZ=0
    g50: LineSegment StartX=12.75 StartY=-21.6 StartZ=0 EndX=17.25 EndY=-21.6 EndZ=0
    g51: ArcOfCircle CenterX=15 CenterY=-19.6 CenterZ=0 NormalX=0 NormalY=0 NormalZ=1 AngleXU=0 Radius=3.0104 StartAngle=5.55654 EndAngle=7.00983
    g52: ArcOfCircle CenterX=15 CenterY=-29.4 CenterZ=0 NormalX=0 NormalY=0 NormalZ=1 AngleXU=0 Radius=3.0104 StartAngle=2.41495 EndAngle=3.86823
    g53: LineSegment StartX=12.75 StartY=-27.4 StartZ=0 EndX=17.25 EndY=-27.4 EndZ=0
    g54: LineSegment StartX=12.75 StartY=-31.4 StartZ=0 EndX=17.25 EndY=-31.4 EndZ=0
    g55: ArcOfCircle CenterX=15 CenterY=-29.4 CenterZ=0 NormalX=0 NormalY=0 NormalZ=1 AngleXU=0 Radius=3.0104 StartAngle=5.55654 EndAngle=7.00983
  constraints (182):
    c: Horizontal(g1)
    c: Horizontal(g2)
    c: PointOnObject(g1,g0)
    c: Coincident(g0,g3)
    c: Coincident(g0,g2)
    c: Coincident(g3,g2)
    c: Coincident(g1,g0)
    c: Coincident(g3,g1)
    c: Equal(g2,g1)
    c: DistanceY(g2,g1) = 4
    c: Horizontal(g5)
    c: Horizontal(g6)
    c: PointOnObject(g5,g4)
    c: Coincident(g4,g7)
    c: Coincident(g4,g6)
    c: Coincident(g7,g6)
    c: Coincident(g5,g4)
    c: Coincident(g7,g5)
    c: Equal(g6,g5)
    c: DistanceY(g6,g5) = 4
    c: Horizontal(g9)
    c: Horizontal(g10)
    c: PointOnObject(g9,g8)
    c: Coincident(g8,g11)
    c: Coincident(g8,g10)
    c: Coincident(g11,g10)
    c: Coincident(g9,g8)
    c: Coincident(g11,g9)
    c: Equal(g10,g9)
    c: DistanceY(g10,g9) = 4
    c: Horizontal(g13)
    c: Horizontal(g14)
    c: PointOnObject(g13,g12)
    c: Coincident(g12,g15)
    c: Coincident(g12,g14)
    c: Coincident(g15,g14)
    c: Coincident(g13,g12)
    c: Coincident(g15,g13)
    c: Equal(g14,g13)
    c: DistanceY(g14,g13) = 4
    c: Horizontal(g17)
    c: Horizontal(g18)
    c: PointOnObject(g17,g16)
    c: Coincident(g16,g19)
    c: Coincident(g16,g18)
    c: Coincident(g19,g18)
    c: Coincident(g17,g16)
    c: Coincident(g19,g17)
    c: Equal(g18,g17)
    c: DistanceY(g18,g17) = 4
    c: Horizontal(g21)
    c: Horizontal(g22)
    c: PointOnObject(g21,g20)
    c: Coincident(g20,g23)
    c: Coincident(g20,g22)
    c: Coincident(g23,g22)
    c: Coincident(g21,g20)
    c: Coincident(g23,g21)
    c: Equal(g22,g21)
    c: DistanceY(g22,g21) = 4
    c: Horizontal(g25)
    c: Horizontal(g26)
    c: PointOnObject(g25,g24)
    c: Coincident(g24,g27)
    c: Coincident(g24,g26)
    c: Coincident(g27,g26)
    c: Coincident(g25,g24)
    c: Coincident(g27,g25)
    c: Equal(g26,g25)
    c: DistanceY(g26,g25) = 4
    c: Vertical(g0,g4)
    c: Vertical(g4,g8)
    c: Vertical(g8,g12)
    c: Vertical(g12,g16)
    c: Vertical(g16,g20)
    c: Vertical(g20,g24)
    c: Equal(g2,g18)
    c: Equal(g18,g22)
    c: Equal(g22,g26)
    c: Equal(g1,g5)
    c: Equal(g5,g9)
    c: Equal(g9,g13)
    c: DistanceY(g8,g12) = 9.8
    c: DistanceY(g4,g8) = 9.8
    c: DistanceY(g0,g4) = 9.8
    c: DistanceY(g16,g0) = 9.8
    c: DistanceY(g20,g16) = 9.8
    c: DistanceY(g24,g20) = 9.8
    c: PointOnObject(g0,g-1)
    c: Horizontal(g29)
    c: Horizontal(g30)
    c: PointOnObject(g29,g28)
    c: Coincident(g28,g31)
    c: Coincident(g28,g30)
    c: Coincident(g31,g30)
    c: Coincident(g29,g28)
    c: Coincident(g31,g29)
    c: Equal(g30,g29)
    c: DistanceY(g30,g29) = 4
    c: Horizontal(g33)
    c: Horizontal(g34)
    c: PointOnObject(g33,g32)
    c: Coincident(g32,g35)
    c: Coincident(g32,g34)
    c: Coincident(g35,g34)
    c: Coincident(g33,g32)
    c: Coincident(g35,g33)
    c: Equal(g34,g33)
    c: DistanceY(g34,g33) = 4
    c: Horizontal(g37)
    c: Horizontal(g38)
    c: PointOnObject(g37,g36)
    c: Coincident(g36,g39)
    c: Coincident(g36,g38)
    c: Coincident(g39,g38)
    c: Coincident(g37,g36)
    c: Coincident(g39,g37)
    c: Equal(g38,g37)
    c: DistanceY(g38,g37) = 4
    c: Horizontal(g41)
    c: Horizontal(g42)
    c: PointOnObject(g41,g40)
    c: Coincident(g40,g43)
    c: Coincident(g40,g42)
    c: Coincident(g43,g42)
    c: Coincident(g41,g40)
    c: Coincident(g43,g41)
    c: Equal(g42,g41)
    c: DistanceY(g42,g41) = 4
    c: Horizontal(g45)
    c: Horizontal(g46)
    c: PointOnObject(g45,g44)
    c: Coincident(g44,g47)
    c: Coincident(g44,g46)
    c: Coincident(g47,g46)
    c: Coincident(g45,g44)
    c: Coincident(g47,g45)
    c: Equal(g46,g45)
    c: DistanceY(g46,g45) = 4
    c: Horizontal(g49)
    c: Horizontal(g50)
    c: PointOnObject(g49,g48)
    c: Coincident(g48,g51)
    c: Coincident(g48,g50)
    c: Coincident(g51,g50)
    c: Coincident(g49,g48)
    c: Coincident(g51,g49)
    c: Equal(g50,g49)
    c: DistanceY(g50,g49) = 4
    c: Horizontal(g53)
    c: Horizontal(g54)
    c: PointOnObject(g53,g52)
    c: Coincident(g52,g55)
    c: Coincident(g52,g54)
    c: Coincident(g55,g54)
    c: Coincident(g53,g52)
    c: Coincident(g55,g53)
    c: Equal(g54,g53)
    c: DistanceY(g54,g53) = 4
    c: Vertical(g28,g32)
    c: Vertical(g32,g36)
    c: Vertical(g36,g40)
    c: Vertical(g40,g44)
    c: Vertical(g44,g48)
    c: Vertical(g48,g52)
    c: Equal(g30,g46)
    c: Equal(g46,g50)
    c: Equal(g50,g54)
    c: Equal(g29,g33)
    c: Equal(g33,g37)
    c: Equal(g37,g41)
    c: DistanceY(g36,g40) = 9.8
    c: DistanceY(g32,g36) = 9.8
    c: DistanceY(g28,g32) = 9.8
    c: DistanceY(g44,g28) = 9.8
    c: DistanceY(g48,g44) = 9.8
    c: DistanceY(g52,g48) = 9.8
    c: PointOnObject(g28,g-1)
    c: DistanceX(g24,g26) = 4.5
    c: DistanceX(g52,g54) = 4.5
    c: DistanceX(g-1,g28) = 15
    c: DistanceX(g28,g0) = 14
FEATURE [PartDesign::Pocket] Pocket  label="PiercesPocket"
  BaseFeature = -> Pad
  Direction = (-2e-16,2e-16,1)
  Length = 69.4
  Length2 = 5
  Midplane = true
  Profile = -> Sketch
  ReferenceAxis = -> Sketch [N_Axis]
  Type = 0
  expr: Length = Spreadsheet.mmBaseWidth + Spreadsheet.mmCellWall * 2
FEATURE [PartDesign::Body] Body004  label="BeamFixator"
  Group = -> [Sketch022,Pad,Sketch,Pocket]
  Origin = -> Origin005
  Tip = -> Pocket
COMPONENT P3 — recipe-attached ("HingePart", modeled in this document).
Construction recipe (the document's own serialized feature program — sketch geometry with constraints, then the solid features built on it; lengths are millimeters unless a unit is written):

FEATURE [PartDesign::LinearPattern] LinearPattern
  Direction = -> Sketch007 [V_Axis]
  Length = 67.8
  Occurrences = 4
  Originals = -> [Revolution,Revolution004,Pocket001,Pocket002,Pad008,Pad009,Pad010,Pad011,Pocket004,Pocket005]
  expr: Length = Spreadsheet.mmHingeHight
  expr: Occurrences = Spreadsheet.nHingeHightDiskCnt
FEATURE [PartDesign::Body] Body005
  Group = -> [LinearPattern]
  Origin = -> Origin007
  Tip = -> LinearPattern
COMPONENT P4 — recipe-attached ("PetalMountingTemplate", modeled in this document).
Construction recipe (the document's own serialized feature program — sketch geometry with constraints, then the solid features built on it; lengths are millimeters unless a unit is written):

FEATURE [Sketcher::SketchObject] Sketch035  label="CommonFixatorScatch001"
  AttachmentOffset = pos=(0,0,16.32) rot=(0,0,1;0rad)
  FullyConstrained = false
  MapMode = 5
  Placement = pos=(16.32,-3.6e-15,3.6e-15) rot=(0.57735,0.57735,0.57735;2.0944rad)
  Support = -> [YZ_Plane013]
  expr: .AttachmentOffset.Base.z = Spreadsheet.mmFixatorHight * 0.8
  expr: Constraints[0] = Spreadsheet.mmAxisTubeDia + 2 * Spreadsheet.mmFixatorThick
  expr: Constraints[24] = Spreadsheet.mmBaseWidth
  expr: Constraints[3] = Spreadsheet.mmAxisTubeDia
  sketch-geometry (9):
    g0: Circle CenterX=0 CenterY=0 CenterZ=0 NormalX=0 NormalY=0 NormalZ=1 AngleXU=0 Radius=26.62
    g1: LineSegment StartX=0 StartY=0 StartZ=0 EndX=49.303 EndY=28.4651 EndZ=0
    g2: ArcOfCircle CenterX=0 CenterY=0 CenterZ=0 NormalX=0 NormalY=0 NormalZ=1 AngleXU=0 Radius=20.4 StartAngle=4.71235 EndAngle=6.7955
    g3: LineSegment StartX=0 StartY=-20.4 StartZ=0 EndX=0 EndY=-39.1443 EndZ=0
    g4: LineSegment StartX=0 StartY=-39.1443 StartZ=0 EndX=6.1036 EndY=-42.6683 EndZ=0
    g5: LineSegment StartX=6.1036 StartY=-42.6683 StartZ=0 EndX=40.0036 EndY=16.0483 EndZ=0
    g6: LineSegment StartX=40.0036 StartY=16.0483 StartZ=0 EndX=33.9 EndY=19.5722 EndZ=0
    g7: LineSegment StartX=33.9 StartY=19.5722 StartZ=0 EndX=17.6669 EndY=10.2 EndZ=0
    g8: ArcOfCircle CenterX=0 CenterY=0 CenterZ=0 NormalX=0 NormalY=0 NormalZ=1 AngleXU=0 Radius=20.4 StartAngle=4.71239 EndAngle=6.80678
  constraints (25):
    c: Diameter(g0) = 53.24
    c: Angle(g-1,g1) = 0.523599
    c: PointOnObject(g6,g1)
    c: Diameter(g2) = 40.8
    c: Vertical(g3)
    c: Coincident(g3,g4)
    c: Coincident(g4,g5)
    c: Coincident(g5,g6)
    c: Coincident(g6,g7)
    c: PointOnObject(g3,g-2)
    c: Parallel(g4,g6)
    c: Perpendicular(g5,g4)
    c: Tangent(g0,g5)
    c: PointOnObject(g8,g1)
    c: Coincident(g8,g7)
    c: PointOnObject(g8,g-2)
    c: PointOnObject(g8,g-1)
    c: PointOnObject(g8,g2)
    c: Coincident(g3,g8)
    c: Equal(g4,g6)
    c: Equal(g7,g3)
    c: Coincident(g2,g1)
    c: Coincident(g8,g1)
    c: Coincident(g8,g0)
    c: Distance(g4,g5) = 67.8
FEATURE [PartDesign::Pad] Pad013  label="AxisFixatorBodyPad001"
  Direction = (1,-2e-16,3e-16)
  Length = 6.12
  Length2 = 10
  Placement = pos=(0,0,0) rot=(0.57735,0.57735,0.57735;2.0944rad)
  Profile = -> Sketch035
  ReferenceAxis = -> Sketch035 [N_Axis]
  Type = 0
  expr: Length = Spreadsheet.mmFixatorHight * 0.3
FEATURE [Sketcher::SketchObject] Sketch038  label="MaxPetalBase004"
  FullyConstrained = false
  MapMode = 5
  Placement = pos=(0,0,0) rot=(0.57735,0.57735,0.57735;2.0944rad)
  Support = -> [YZ_Plane013]
  expr: Constraints[0] = Spreadsheet.mmAxisTubeDia + 2 * Spreadsheet.mmFixatorThick
  expr: Constraints[10] = Spreadsheet.mmAxisTubeDia
  expr: Constraints[15] = Spreadsheet.mmPetalPocketWidth
  expr: Constraints[1] = Spreadsheet.mmAxisTubeDia
  expr: Constraints[6] = Spreadsheet.mmAxisTubeDia * 2
  sketch-geometry (7):
    g0: Circle CenterX=0 CenterY=2.5e-15 CenterZ=0 NormalX=0 NormalY=0 NormalZ=1 AngleXU=0 Radius=39.855
    g1: Circle CenterX=0 CenterY=-1.1e-15 CenterZ=0 NormalX=0 NormalY=0 NormalZ=1 AngleXU=0 Radius=26.62
    g2: ArcOfCircle CenterX=0 CenterY=2.5e-15 CenterZ=0 NormalX=0 NormalY=0 NormalZ=1 AngleXU=0 Radius=20.4 StartAngle=5.6709 EndAngle=6.80795
    g3: LineSegment StartX=19.5933 StartY=5.67991 StartZ=0 EndX=81.6 EndY=5.67991 EndZ=0
    g4: LineSegment StartX=81.6 StartY=5.67991 StartZ=0 EndX=81.6 EndY=-5.67991 EndZ=0
    g5: LineSegment StartX=81.6 StartY=-5.67991 StartZ=0 EndX=19.5933 EndY=-5.67991 EndZ=0
    g6: ArcOfCircle CenterX=0 CenterY=2.5e-15 CenterZ=0 NormalX=0 NormalY=0 NormalZ=1 AngleXU=0 Radius=20.4 StartAngle=6.00103 EndAngle=6.56534
  constraints (16):
    c: Diameter(g1) = 53.24
    c: Diameter(g2) = 40.8
    c: Coincident(g3,g4)
    c: Coincident(g4,g5)
    c: Coincident(g0,g2)
    c: Vertical(g4)
    c: DistanceX(g-1,g4) = 81.6
    c: Coincident(g6,g0)
    c: Coincident(g6,g3)
    c: Coincident(g6,g5)
    c: Diameter(g6) = 40.8
    c: Horizontal(g3)
    c: Horizontal(g5)
    c: PointOnObject(g6,g-2)
    c: Symmetric(g3,g5,g-1)
    c: DistanceY(g5,g3) = 11.3598
FEATURE [Sketcher::SketchObject] Sketch039  label="MinPetalBase003"
  AttachmentOffset = pos=(0,0,20.4) rot=(0,0,1;0rad)
  FullyConstrained = false
  MapMode = 5
  Placement = pos=(20.4,-4.5e-15,4.5e-15) rot=(0.57735,0.57735,0.57735;2.0944rad)
  Support = -> [YZ_Plane013]
  expr: .AttachmentOffset.Base.z = Spreadsheet.mmFixatorHight
  expr: Constraints[0] = Spreadsheet.mmAxisTubeDia + 2 * Spreadsheet.mmFixatorThick
  expr: Constraints[10] = Spreadsheet.mmAxisTubeDia
  expr: Constraints[11] = Spreadsheet.mmPetalPocketWidth
  expr: Constraints[1] = Spreadsheet.mmAxisTubeDia
  expr: Constraints[6] = Spreadsheet.mmAxisTubeDia * 2
  sketch-geometry (7):
    g0: Circle CenterX=0 CenterY=2.1e-15 CenterZ=0 NormalX=0 NormalY=0 NormalZ=1 AngleXU=0 Radius=39.844
    g1: Circle CenterX=0 CenterY=2.1e-15 CenterZ=0 NormalX=0 NormalY=0 NormalZ=1 AngleXU=0 Radius=26.62
    g2: ArcOfCircle CenterX=0 CenterY=2.1e-15 CenterZ=0 NormalX=0 NormalY=0 NormalZ=1 AngleXU=0 Radius=20.4 StartAngle=3.90517 EndAngle=6.76925
    g3: LineSegment StartX=19.5933 StartY=5.67991 StartZ=0 EndX=81.6 EndY=5.67991 EndZ=0
    g4: LineSegment StartX=81.6 StartY=5.67991 StartZ=0 EndX=81.6 EndY=-5.67991 EndZ=0
    g5: LineSegment StartX=81.6 StartY=-5.67991 StartZ=0 EndX=19.5933 EndY=-5.67991 EndZ=0
    g6: ArcOfCircle CenterX=0 CenterY=2.1e-15 CenterZ=0 NormalX=0 NormalY=0 NormalZ=1 AngleXU=0 Radius=20.4 StartAngle=6.00103 EndAngle=6.56534
  constraints (17):
    c: Diameter(g1) = 53.24
    c: Diameter(g2) = 40.8
    c: Coincident(g3,g4)
    c: Coincident(g4,g5)
    c: Coincident(g0,g2)
    c: Vertical(g4)
    c: DistanceX(g-1,g4) = 81.6
    c: Coincident(g6,g0)
    c: Coincident(g6,g3)
    c: Coincident(g6,g5)
    c: Diameter(g6) = 40.8
    c: DistanceY(g5,g3) = 11.3598
    c: Symmetric(g3,g5,g-1)
    c: Coincident(g1,g6)
    c: Coincident(g-1,g6)
    c: Horizontal(g3)
    c: Horizontal(g5)
FEATURE [PartDesign::SubtractiveLoft] SubtractiveLoft001  label="PetalBodySubtractiveLoft001"
  BaseFeature = -> Pad013
  Closed = false
  Placement = pos=(0,0,0) rot=(0.57735,0.57735,0.57735;2.0944rad)
  Profile = -> Sketch038
  Ruled = false
  Sections = -> [Sketch039]
FEATURE [PartDesign::PolarPattern] PolarPattern001  label="ExisFixatorBodyPolarPattern001"
  Angle = 360
  Axis = -> Sketch035 [N_Axis]
  BaseFeature = -> SubtractiveLoft001
  Occurrences = 3
  Originals = -> [Pad013,SubtractiveLoft001]
  Placement = pos=(0,0,0) rot=(0.57735,0.57735,0.57735;2.0944rad)
FEATURE [Sketcher::SketchObject] Sketch040  label="CommonFixatorScatch002"
  AttachmentOffset = pos=(0,0,16.32) rot=(0,0,1;0rad)
  FullyConstrained = true
  MapMode = 5
  Placement = pos=(16.32,-3.6e-15,3.6e-15) rot=(0.57735,0.57735,0.57735;2.0944rad)
  Support = -> [YZ_Plane013]
  expr: .AttachmentOffset.Base.z = Spreadsheet.mmFixatorHight * 0.8
  expr: Constraints[11] = Spreadsheet.mmAxisTubeDia * 2
  expr: Constraints[14] = Spreadsheet.mmTemplatePartsConnectorDia - 2 * Spreadsheet.mmAirSpace
  expr: Constraints[15] = Spreadsheet.mmTemplatePartsConnectorDia * 3 / 2
  expr: Constraints[1] = Spreadsheet.mmAxisTubeDia + 2 * Spreadsheet.mmFixatorThick
  expr: Constraints[27] = Spreadsheet.mmAirSpace
  expr: Constraints[33] = Spreadsheet.mmTemplatePartsConnectorDia / 3
  expr: Constraints[41] = Spreadsheet.mmTemplatePartsConnectorDia
  expr: Constraints[43] = Spreadsheet.mmTemplatePartsConnectorDia * 2 / 3
  expr: Constraints[45] = Spreadsheet.mmTemplatePartsConnectorDia * 2 / 3 - 2 * Spreadsheet.mmAirSpace
  expr: Constraints[52] = Spreadsheet.mmTemplatePartsConnectorDia / 3
  expr: Constraints[55] = Spreadsheet.mmTemplatePartsConnectorDia / 2
  sketch-geometry (19):
    g0: Circle CenterX=0 CenterY=0 CenterZ=0 NormalX=0 NormalY=0 NormalZ=1 AngleXU=0 Radius=40.8
    g1: Circle CenterX=0 CenterY=0 CenterZ=0 NormalX=0 NormalY=0 NormalZ=1 AngleXU=0 Radius=26.62
    g2: LineSegment StartX=-35.5321 StartY=20.0526 StartZ=0 EndX=-28.3499 EndY=15.9059 EndZ=0
    g3: LineSegment StartX=22.767 StartY=-13.6064 StartZ=0 EndX=23.167 EndY=-12.9136 EndZ=0
    g4: LineSegment StartX=23.167 StartY=-12.9136 StartZ=0 EndX=21.4554 EndY=-11.9254 EndZ=0
    g5: LineSegment StartX=-35.1321 StartY=20.7454 StartZ=0 EndX=-35.5321 EndY=20.0526 EndZ=0
    g6: LineSegment StartX=23.0536 StartY=-13.31 StartZ=0 EndX=-35.3338 EndY=20.4 EndZ=0
    g7: ArcOfCircle CenterX=-26.42 CenterY=17.1754 CenterZ=0 NormalX=0 NormalY=0 NormalZ=1 AngleXU=0 Radius=2.31 StartAngle=4.65418 EndAngle=10.0066
    g8: LineSegment StartX=-26.5543 StartY=14.8693 StartZ=0 EndX=18.3629 EndY=-11.0637 EndZ=0
    g9: LineSegment StartX=-29.5129 StartY=17.5011 StartZ=0 EndX=-35.1321 EndY=20.7454 EndZ=0
    g10: LineSegment StartX=-35.1321 StartY=20.7454 StartZ=0 EndX=-35.5321 EndY=20.0526 EndZ=0
    g11: LineSegment StartX=-35.5321 StartY=20.0526 StartZ=0 EndX=22.851 EndY=-13.6549 EndZ=0
    g12: LineSegment StartX=22.851 StartY=-13.6549 StartZ=0 EndX=23.251 EndY=-12.9621 EndZ=0
    g13: LineSegment StartX=23.251 StartY=-12.9621 StartZ=0 EndX=-35.1321 EndY=20.7454 EndZ=0
    g14: ArcOfCircle CenterX=-26.42 CenterY=17.1754 CenterZ=0 NormalX=0 NormalY=0 NormalZ=1 AngleXU=0 Radius=3.11 StartAngle=5.34093 EndAngle=9.31984
    g15: ArcOfCircle CenterX=20.188 CenterY=-12.0474 CenterZ=0 NormalX=0 NormalY=0 NormalZ=1 AngleXU=0 Radius=2.07333 StartAngle=2.64723 EndAngle=5.73035
    g16: ArcOfCircle CenterX=20.188 CenterY=-12.0474 CenterZ=0 NormalX=0 NormalY=0 NormalZ=1 AngleXU=0 Radius=1.27333 StartAngle=1.99844 EndAngle=6.37914
    g17: LineSegment StartX=21.9524 StartY=-13.1361 StartZ=0 EndX=22.767 EndY=-13.6064 EndZ=0
    g18: LineSegment StartX=19.6599 StartY=-10.8888 StartZ=0 EndX=-24.5914 EndY=14.6597 EndZ=0
  constraints (56):
    c: PointOnObject(g6,g0)
    c: Diameter(g1) = 53.24
    c: Coincident(g0,g1)
    c: Coincident(g0,g-1)
    c: Coincident(g3,g4)
    c: Coincident(g9,g5)
    c: Coincident(g5,g2)
    c: Perpendicular(g3,g2)
    c: Symmetric(g2,g9,g6)
    c: Symmetric(g17,g3,g6)
    c: PointOnObject(g0,g6)
    c: Diameter(g0) = 81.6
    c: PointOnObject(g6,g1)
    c: Angle(g-1,g6) = 2.61799
    c: Diameter(g7) = 4.62
    c: Distance(g7,g5) = 9.33
    c: Parallel(g9,g4)
    c: Parallel(g2,g8)
    c: Coincident(g10,g11)
    c: Coincident(g11,g12)
    c: Coincident(g12,g13)
    c: Coincident(g13,g10)
    c: PointOnObject(g10,g0)
    c: Symmetric(g10,g10,g6)
    c: Parallel(g6,g13)
    c: Parallel(g11,g13)
    c: Coincident(g5,g10)
    c: Distance(g3,g3) = 0.8
    c: Coincident(g3,g17)
    c: PointOnObject(g11,g1)
    c: PointOnObject(g12,g1)
    c: PointOnObject(g3,g13)
    c: Distance(g6,g3) = 0.1
    c: Distance(g2,g8) = 2.07333
    c: PointOnObject(g14,g13)
    c: PointOnObject(g14,g13)
    c: PointOnObject(g18,g14)
    c: PointOnObject(g9,g14)
    c: Coincident(g7,g8)
    c: Coincident(g7,g2)
    c: Coincident(g14,g7)
    c: Diameter(g14) = 6.22
    c: PointOnObject(g18,g13)
    c: Diameter(g15) = 4.14667
    c: Coincident(g15,g16)
    c: Diameter(g16) = 2.54667
    c: Coincident(g15,g8)
    c: PointOnObject(g8,g11)
    c: Coincident(g17,g15)
    c: PointOnObject(g15,g11)
    c: Coincident(g4,g16)
    c: Coincident(g18,g16)
    c: Distance(g16,g4) = 2.07333
    c: PointOnObject(g4,g13)
    c: PointOnObject(g16,g13)
    c: Distance(g15,g12) = 3.11
FEATURE [PartDesign::Pocket] Pocket003
  BaseFeature = -> PolarPattern001
  Direction = (-1,2e-16,-3e-16)
  Length = 40.8
  Length2 = 5
  Midplane = true
  Placement = pos=(0,0,0) rot=(0.57735,0.57735,0.57735;2.0944rad)
  Profile = -> Sketch040
  ReferenceAxis = -> Sketch040 [N_Axis]
  Type = 0
  expr: Length = Spreadsheet.mmAxisTubeDia
FEATURE [PartDesign::Chamfer] Chamfer002
  Angle = 45
  Base = -> Pocket003 [Edge1,Edge35,Edge31,Edge98,Edge94,Edge47,Edge12]
  BaseFeature = -> Pocket003
  ChamferType = 0
  FlipDirection = false
  Placement = pos=(0,0,0) rot=(0.57735,0.57735,0.57735;2.0944rad)
  Size = 1
  Size2 = 1
  SupportTransform = false
  UseAllEdges = false
FEATURE [PartDesign::Chamfer] Chamfer003
  Angle = 45
  Base = -> Chamfer002 [Edge56,Edge17,Edge3,Edge28]
  BaseFeature = -> Chamfer002
  ChamferType = 0
  FlipDirection = false
  Placement = pos=(0,0,0) rot=(0.57735,0.57735,0.57735;2.0944rad)
  Size = 1
  Size2 = 1
  SupportTransform = false
  UseAllEdges = false
FEATURE [PartDesign::Chamfer] Chamfer004
  Angle = 45
  Base = -> Chamfer003 [Edge56,Edge61,Edge130,Edge128,Edge73,Edge75]
  BaseFeature = -> Chamfer003
  ChamferType = 0
  FlipDirection = false
  Placement = pos=(0,0,0) rot=(0.57735,0.57735,0.57735;2.0944rad)
  Size = 1
  Size2 = 1
  SupportTransform = false
  UseAllEdges = false
FEATURE [PartDesign::Fillet] Fillet
  Base = -> Chamfer004 [Edge66,Edge26]
  BaseFeature = -> Chamfer004
  Placement = pos=(0,0,0) rot=(0.57735,0.57735,0.57735;2.0944rad)
  Radius = 1
  SupportTransform = false
  UseAllEdges = false
FEATURE [PartDesign::Body] Body010  label="AxisFixatorTemplate"
  Group = -> [Sketch035,Pad013,Sketch038,Sketch039,SubtractiveLoft001,PolarPattern001,Sketch040,Pocket003,Chamfer002,Chamfer003,Chamfer004,Fillet]
  Origin = -> Origin019
  Tip = -> Fillet
COMPONENT P5 — recipe-attached ("AxisFixatorAbsolete", modeled in this document).
Construction recipe (the document's own serialized feature program — sketch geometry with constraints, then the solid features built on it; lengths are millimeters unless a unit is written):

FEATURE [Sketcher::SketchObject] Sketch041  label="CommonFixatorScatch003"
  FullyConstrained = false
  MapMode = 5
  Placement = pos=(0,0,0) rot=(0.57735,0.57735,0.57735;2.0944rad)
  Support = -> [YZ_Plane013]
  expr: Constraints[22] = 2 * (Spreadsheet.mmAxisTubeDia / 2 + Spreadsheet.mmFixatorThick) / cos(Spreadsheet.angPetal / 2)
  expr: Constraints[23] = Spreadsheet.mmHingeHight
  expr: Constraints[31] = Spreadsheet.mmAxisTubeDia
  expr: Constraints[64] = Spreadsheet.mmPetalWidth + Spreadsheet.mmAirSpace
  expr: Constraints[67] = Spreadsheet.mmAxisTubeDia / 2 + Spreadsheet.mmPetalHightMax + Spreadsheet.mmTwoSideTapeThick + Spreadsheet.mmAirSpace
  sketch-geometry (24):
    g0: LineSegment StartX=33.9 StartY=19.5722 StartZ=0 EndX=-33.9 EndY=19.5722 EndZ=0
    g1: LineSegment StartX=-33.9 StartY=19.5722 StartZ=0 EndX=0 EndY=-39.1443 EndZ=0
    g2: LineSegment StartX=0 StartY=-39.1443 StartZ=0 EndX=33.9 EndY=19.5722 EndZ=0
    g3: Circle CenterX=0 CenterY=0 CenterZ=0 NormalX=0 NormalY=0 NormalZ=1 AngleXU=0 Radius=39.1443
    g4: LineSegment StartX=-23.8668 StartY=13.7795 StartZ=0 EndX=-23.8668 EndY=-13.7795 EndZ=0
    g5: LineSegment StartX=-23.8668 StartY=-13.7795 StartZ=0 EndX=0 EndY=-27.5591 EndZ=0
    g6: LineSegment StartX=0 StartY=-27.5591 StartZ=0 EndX=23.8668 EndY=-13.7795 EndZ=0
    g7: LineSegment StartX=23.8668 StartY=-13.7795 StartZ=0 EndX=23.8668 EndY=13.7795 EndZ=0
    g8: LineSegment StartX=23.8668 StartY=13.7795 StartZ=0 EndX=0 EndY=27.5591 EndZ=0
    g9: LineSegment StartX=-1e-16 StartY=27.5591 StartZ=0 EndX=-23.8668 EndY=13.7795 EndZ=0
    g10: Circle CenterX=0 CenterY=0 CenterZ=0 NormalX=0 NormalY=0 NormalZ=1 AngleXU=0 Radius=27.5591
    g11: LineSegment StartX=0 StartY=0 StartZ=0 EndX=33.9 EndY=19.5722 EndZ=0
    g12: ArcOfCircle CenterX=0 CenterY=0 CenterZ=0 NormalX=0 NormalY=0 NormalZ=1 AngleXU=0 Radius=20.4 StartAngle=4.5996 EndAngle=6.79538
    g13: LineSegment StartX=0 StartY=-20.4 StartZ=0 EndX=0 EndY=-39.1443 EndZ=0
    g14: LineSegment StartX=0 StartY=-39.1443 StartZ=0 EndX=6.91684 EndY=-43.1378 EndZ=0
    g15: LineSegment StartX=6.91684 StartY=-43.1378 StartZ=0 EndX=40.8168 EndY=15.5787 EndZ=0
    g16: LineSegment StartX=40.8168 StartY=15.5787 StartZ=0 EndX=33.9 EndY=19.5722 EndZ=0
    g17: LineSegment StartX=33.9 StartY=19.5722 StartZ=0 EndX=17.6669 EndY=10.2 EndZ=0
    g18: LineSegment StartX=14.7156 StartY=-14.1284 StartZ=0 EndX=18.6289 EndY=-20.9065 EndZ=0
    g19: LineSegment StartX=18.6289 StartY=-20.9065 StartZ=0 EndX=8.79105 EndY=-26.5864 EndZ=0
    g20: LineSegment StartX=8.79105 StartY=-26.5864 StartZ=0 EndX=4.87772 EndY=-19.8083 EndZ=0
    g21: ArcOfCircle CenterX=0 CenterY=0 CenterZ=0 NormalX=0 NormalY=0 NormalZ=1 AngleXU=0 Radius=20.4 StartAngle=4.71239 EndAngle=4.95383
    g22: ArcOfCircle CenterX=0 CenterY=0 CenterZ=0 NormalX=0 NormalY=0 NormalZ=1 AngleXU=0 Radius=20.4 StartAngle=5.51814 EndAngle=6.80678
    g23: LineSegment StartX=0 StartY=0 StartZ=0 EndX=19.5722 EndY=-33.9 EndZ=0
  constraints (64):
    c: Coincident(g0,g1)
    c: Coincident(g1,g2)
    c: Coincident(g2,g0)
    c: Equal(g0,g1)
    c: Equal(g0,g2)
    c: PointOnObject(g0,g3)
    c: Coincident(g4,g5)
    c: Coincident(g5,g6)
    c: Coincident(g6,g7)
    c: Coincident(g7,g8)
    c: Coincident(g8,g9)
    c: Coincident(g9,g4)
    c: Equal(g4, g5-g9) x5
    c: PointOnObject(g4,g10)
    c: PointOnObject(g5,g10)
    c: PointOnObject(g6,g10)
    c: PointOnObject(g7,g10)
    c: PointOnObject(g8,g10)
    c: Diameter(g10) = 55.1181
    c: Distance(g2) = 67.8
    c: PointOnObject(g5,g-2)
    c: PointOnObject(g4,g10)
    c: Angle(g-1,g11) = 0.523599
    c: Coincident(g3,g10)
    c: Coincident(g3,g11)
    c: Coincident(g3,g-1)
    c: PointOnObject(g0,g11)
    c: Diameter(g12) = 40.8
    c: Coincident(g12,g3)
    c: Vertical(g13)
    c: Coincident(g13,g14)
    c: Coincident(g14,g15)
    c: Coincident(g15,g16)
    c: Coincident(g16,g17)
    c: Coincident(g19,g20)
    c: Coincident(g1,g13)
    c: Coincident(g0,g16)
    c: Equal(g12,g21)
    c: Coincident(g12,g21)
    c: PointOnObject(g13,g-2)
    c: PointOnObject(g13,g3)
    c: Parallel(g2,g15)
    c: Parallel(g14,g16)
    c: Perpendicular(g15,g14)
    c: Tangent(g10,g15)
    c: PointOnObject(g11,g3)
    c: Coincident(g21,g22)
    c: PointOnObject(g17,g11)
    c: Coincident(g20,g21)
    c: Coincident(g21,g13)
    c: Coincident(g22,g18)
    c: PointOnObject(g22,g11)
    c: Coincident(g22,g17)
    c: PointOnObject(g17,g11)
    c: Perpendicular(g20,g19)
    c: Perpendicular(g19,g18)
    c: Coincident(g23,g21)
    c: Angle(g23,g-2) = 2.61799
    c: PointOnObject(g23,g3)
    c: Symmetric(g20,g18,g23)
    c: Distance(g20,g18) = 11.3598
    c: Perpendicular(g23,g19)
    c: Coincident(g18,g19)
    c: Distance(g21,g19) = 27.42
FEATURE [PartDesign::Pad] Pad014  label="AxisFixatorBodyPad002"
  Direction = (1,-2e-16,3e-16)
  Length = 20.4
  Length2 = 10
  Placement = pos=(0,0,0) rot=(0.57735,0.57735,0.57735;2.0944rad)
  Profile = -> Sketch041
  ReferenceAxis = -> Sketch041 [N_Axis]
  Type = 0
  expr: Length = Spreadsheet.mmFixatorHight
FEATURE [Sketcher::SketchObject] Sketch044  label="MaxPetalBase006"
  FullyConstrained = false
  MapMode = 5
  Placement = pos=(0,0,0) rot=(0.57735,0.57735,0.57735;2.0944rad)
  Support = -> [YZ_Plane013]
  expr: Constraints[0] = Spreadsheet.mmAxisTubeDia + 2 * Spreadsheet.mmFixatorThick
  expr: Constraints[14] = Spreadsheet.mmPetalWidth + Spreadsheet.mmAirSpace
  expr: Constraints[1] = Spreadsheet.mmAxisTubeDia
  expr: Constraints[5] = Spreadsheet.mmAxisTubeDia / 2 + Spreadsheet.mmPetalHightMax
  expr: Constraints[9] = Spreadsheet.mmAxisTubeDia
  sketch-geometry (7):
    g0: Circle CenterX=0 CenterY=0 CenterZ=0 NormalX=0 NormalY=0 NormalZ=1 AngleXU=0 Radius=39.855
    g1: Circle CenterX=0 CenterY=0 CenterZ=0 NormalX=0 NormalY=0 NormalZ=1 AngleXU=0 Radius=26.62
    g2: ArcOfCircle CenterX=0 CenterY=0 CenterZ=0 NormalX=0 NormalY=0 NormalZ=1 AngleXU=0 Radius=20.4 StartAngle=5.86249 EndAngle=6.74499
    g3: LineSegment StartX=19.5933 StartY=5.67991 StartZ=0 EndX=26.52 EndY=5.67991 EndZ=0
    g4: LineSegment StartX=26.52 StartY=5.67991 StartZ=0 EndX=26.52 EndY=-5.67991 EndZ=0
    g5: LineSegment StartX=26.52 StartY=-5.67991 StartZ=0 EndX=19.5933 EndY=-5.67991 EndZ=0
    g6: ArcOfCircle CenterX=0 CenterY=0 CenterZ=0 NormalX=0 NormalY=0 NormalZ=1 AngleXU=0 Radius=20.4 StartAngle=6.00103 EndAngle=6.56534
  constraints (22):
    c: Diameter(g1) = 53.24
    c: Diameter(g2) = 40.8
    c: Coincident(g3,g4)
    c: Coincident(g4,g5)
    c: Coincident(g0,g2)
    c: DistanceX(g-1,g4) = 26.52
    c: Coincident(g6,g0)
    c: Coincident(g6,g3)
    c: Coincident(g6,g5)
    c: Diameter(g6) = 40.8
    c: Coincident(g6,g-1)
    c: Symmetric(g3,g5,g-1)
    c: Horizontal(g5)
    c: Horizontal(g3)
    c: DistanceY(g5,g3) = 11.3598
    c: Coincident(g6,g1)
    c: PointOnObject(g6,g-2)
    c: PointOnObject(g6,g-1)
    c: PointOnObject(g6,g5)
    c: PointOnObject(g6,g3)
    c: PointOnObject(g3,g6)
    c: Vertical(g4)
FEATURE [Sketcher::SketchObject] Sketch045  label="MinPetalBase005"
  AttachmentOffset = pos=(0,0,18.36) rot=(0,0,1;0rad)
  FullyConstrained = false
  MapMode = 5
  Placement = pos=(18.36,-4.1e-15,4.1e-15) rot=(0.57735,0.57735,0.57735;2.0944rad)
  Support = -> [YZ_Plane013]
  expr: .AttachmentOffset.Base.z = Spreadsheet.mmFixatorHight * 0.9
  expr: Constraints[0] = Spreadsheet.mmAxisTubeDia + 2 * Spreadsheet.mmFixatorThick
  expr: Constraints[10] = Spreadsheet.mmAxisTubeDia
  expr: Constraints[12] = Spreadsheet.mmPetalWidth + Spreadsheet.mmAirSpace
  expr: Constraints[1] = Spreadsheet.mmAxisTubeDia
  expr: Constraints[6] = Spreadsheet.mmAxisTubeDia / 2 + Spreadsheet.mmPetalHightMin
  sketch-geometry (7):
    g0: Circle CenterX=0 CenterY=2.3e-15 CenterZ=0 NormalX=0 NormalY=0 NormalZ=1 AngleXU=0 Radius=39.844
    g1: Circle CenterX=0 CenterY=2.3e-15 CenterZ=0 NormalX=0 NormalY=0 NormalZ=1 AngleXU=0 Radius=26.62
    g2: ArcOfCircle CenterX=0 CenterY=2.3e-15 CenterZ=0 NormalX=0 NormalY=0 NormalZ=1 AngleXU=0 Radius=20.4 StartAngle=3.8687 EndAngle=6.82101
    g3: LineSegment StartX=19.5933 StartY=5.67991 StartZ=0 EndX=23.46 EndY=5.67991 EndZ=0
    g4: LineSegment StartX=23.46 StartY=5.67991 StartZ=0 EndX=23.46 EndY=-5.67991 EndZ=0
    g5: LineSegment StartX=23.46 StartY=-5.67991 StartZ=0 EndX=19.5933 EndY=-5.67991 EndZ=0
    g6: ArcOfCircle CenterX=0 CenterY=2.3e-15 CenterZ=0 NormalX=0 NormalY=0 NormalZ=1 AngleXU=0 Radius=20.4 StartAngle=6.00103 EndAngle=6.56534
  constraints (17):
    c: Diameter(g1) = 53.24
    c: Diameter(g2) = 40.8
    c: Coincident(g3,g4)
    c: Coincident(g4,g5)
    c: Coincident(g0,g2)
    c: Vertical(g4)
    c: DistanceX(g-1,g4) = 23.46
    c: Coincident(g6,g0)
    c: Coincident(g6,g3)
    c: Coincident(g6,g5)
    c: Diameter(g6) = 40.8
    c: Symmetric(g3,g5,g-1)
    c: DistanceY(g5,g3) = 11.3598
    c: Horizontal(g3)
    c: Horizontal(g5)
    c: Coincident(g6,g1)
    c: Coincident(g6,g-1)
FEATURE [PartDesign::SubtractiveLoft] SubtractiveLoft002  label="PetalBodySubtractiveLoft002"
  BaseFeature = -> Pad014
  Closed = false
  Placement = pos=(0,0,0) rot=(0.57735,0.57735,0.57735;2.0944rad)
  Profile = -> Sketch044
  Ruled = false
  Sections = -> [Sketch045]
FEATURE [PartDesign::PolarPattern] PolarPattern002  label="ExisFixatorBodyPolarPattern002"
  Angle = 360
  Axis = -> Sketch041 [N_Axis]
  BaseFeature = -> SubtractiveLoft002
  Occurrences = 3
  Originals = -> [Pad014,SubtractiveLoft002]
  Placement = pos=(0,0,0) rot=(0.57735,0.57735,0.57735;2.0944rad)
FEATURE [PartDesign::Body] Body011  label="AxisFixatorBody001"
  Group = -> [Sketch041,Pad014,Sketch044,Sketch045,SubtractiveLoft002,PolarPattern002]
  Origin = -> Origin021
  Tip = -> PolarPattern002
COMPONENT P6 — recipe-attached ("AxisBodyBandage", modeled in this document).
Construction recipe (the document's own serialized feature program — sketch geometry with constraints, then the solid features built on it; lengths are millimeters unless a unit is written):

FEATURE [Sketcher::SketchObject] Sketch048  label="CommonFixatorScatch004"
  FullyConstrained = false
  MapMode = 5
  Placement = pos=(0,0,0) rot=(0.57735,0.57735,0.57735;2.0944rad)
  Support = -> [YZ_Plane020]
  expr: Constraints[0] = Spreadsheet.mmAxisTubeDia + 2 * Spreadsheet.mmFixatorThick + 2 * Spreadsheet.mmTwoSideTapeThick
  expr: Constraints[13] = <<Spreadsheet>>.mmAxisTubeDia
  expr: Constraints[16] = <<Spreadsheet>>.mmAirSpace
  expr: Constraints[9] = Spreadsheet.mmBaseWidth
  sketch-geometry (21):
    g0: Circle CenterX=0 CenterY=0 CenterZ=0 NormalX=0 NormalY=0 NormalZ=1 AngleXU=0 Radius=26.72
    g1: LineSegment StartX=0 StartY=0 StartZ=0 EndX=33.9 EndY=19.5722 EndZ=0
    g2: LineSegment StartX=-3.7e-15 StartY=-20.4 StartZ=0 EndX=-3.7e-15 EndY=-39.1443 EndZ=0
    g3: LineSegment StartX=-3.7e-15 StartY=-39.1443 StartZ=0 EndX=6.1902 EndY=-42.7183 EndZ=0
    g4: LineSegment StartX=6.1902 StartY=-42.7183 StartZ=0 EndX=40.0902 EndY=15.9983 EndZ=0
    g5: ArcOfCircle CenterX=0 CenterY=0 CenterZ=0 NormalX=0 NormalY=0 NormalZ=1 AngleXU=0 Radius=20.4 StartAngle=4.71239 EndAngle=6.76756
    g6: LineSegment StartX=0 StartY=0 StartZ=0 EndX=20.0617 EndY=-34.7479 EndZ=0
    g7: LineSegment StartX=18.0533 StartY=9.49933 StartZ=0 EndX=34.7 EndY=19.1103 EndZ=0
    g8: LineSegment StartX=33.9 StartY=19.5722 StartZ=0 EndX=40.0902 EndY=15.9983 EndZ=0
    g9: ArcOfCircle CenterX=0 CenterY=0 CenterZ=0 NormalX=0 NormalY=0 NormalZ=1 AngleXU=0 Radius=20.4 StartAngle=4.71239 EndAngle=6.80678
    g10: LineSegment StartX=17.6669 StartY=10.2 StartZ=0 EndX=33.9 EndY=19.5722 EndZ=0
    g11: LineSegment StartX=-3.7e-15 StartY=-39.1443 StartZ=0 EndX=0 EndY=0 EndZ=0
    g12: LineSegment StartX=34.7 StartY=19.1103 StartZ=0 EndX=40.0902 EndY=15.9983 EndZ=0
    g13: Circle CenterX=29.0138 CenterY=9.45344 CenterZ=0 NormalX=0 NormalY=0 NormalZ=1 AngleXU=0 Radius=2
    g14: Circle CenterX=6.32 CenterY=-29.8534 CenterZ=0 NormalX=0 NormalY=0 NormalZ=1 AngleXU=0 Radius=2
    g15: LineSegment StartX=6.32 StartY=-29.8534 StartZ=0 EndX=29.0138 EndY=9.45344 EndZ=0
    g16: LineSegment StartX=0 StartY=0 StartZ=0 EndX=17.6669 EndY=-10.2 EndZ=0
    g17: LineSegment StartX=6.32 StartY=-29.8534 StartZ=0 EndX=0 EndY=-29.8534 EndZ=0
    g18: LineSegment StartX=6.32 StartY=-29.8534 StartZ=0 EndX=11.7933 EndY=-33.0134 EndZ=0
    g19: LineSegment StartX=29.0138 StartY=9.45344 StartZ=0 EndX=25.8538 EndY=14.9267 EndZ=0
    g20: LineSegment StartX=29.0138 StartY=9.45344 StartZ=0 EndX=34.4871 EndY=6.29344 EndZ=0
  constraints (56):
    c: Diameter(g0) = 53.44
    c: Angle(g-1,g1) = 0.523599
    c: Vertical(g2)
    c: Coincident(g2,g3)
    c: Coincident(g3,g4)
    c: PointOnObject(g2,g-2)
    c: Perpendicular(g4,g3)
    c: Tangent(g0,g4)
    c: Angle(g6,g-1) = 1.0472
    c: Distance(g3,g4) = 67.8
    c: Coincident(g-1,g0)
    c: Coincident(g5,g0)
    c: Coincident(g5,g2)
    c: Diameter(g5) = 40.8
    c: Coincident(g1,g5)
    c: Parallel(g7,g1)
    c: Distance(g7,g1) = 0.8
    c: Perpendicular(g8,g4)
    c: Coincident(g8,g4)
    c: PointOnObject(g7,g8)
    c: Coincident(g9,g5)
    c: Coincident(g9,g2)
    c: PointOnObject(g9,g1)
    c: Coincident(g10,g9)
    c: Coincident(g10,g8)
    c: Coincident(g7,g5)
    c: Coincident(g1,g8)
    c: Coincident(g11,g2)
    c: Coincident(g11,g6)
    c: Equal(g11,g1)
    c: Coincident(g6,g5)
    c: Equal(g3,g8)
    c: Coincident(g12,g4)
    c: Coincident(g12,g7)
    c: Equal(g14,g13)
    c: Diameter(g13) = 4
    c: Coincident(g15,g14)
    c: Coincident(g15,g13)
    c: Tangent(g15,g5)
    c: Parallel(g15,g4)
    c: Coincident(g16,g5)
    c: PointOnObject(g16,g5)
    c: Symmetric(g14,g13,g16)
    c: Coincident(g17,g14)
    c: PointOnObject(g17,g2)
    c: Coincident(g18,g14)
    c: PointOnObject(g18,g4)
    c: Coincident(g19,g13)
    c: PointOnObject(g19,g1)
    c: Coincident(g20,g13)
    c: PointOnObject(g20,g4)
    c: Perpendicular(g4,g20)
    c: Equal(g18,g17)
    c: Perpendicular(g4,g18)
    c: Perpendicular(g11,g17)
    c: Perpendicular(g1,g19)
FEATURE [PartDesign::Pad] Pad015
  Direction = (1,-2e-16,3e-16)
  Length = 40.8
  Length2 = 10
  Placement = pos=(0,0,0) rot=(0.57735,0.57735,0.57735;2.0944rad)
  Profile = -> Sketch048
  ReferenceAxis = -> Sketch048 [N_Axis]
  Refine = true
  Reversed = true
  Type = 0
  expr: Length = 2 * Spreadsheet.mmFixatorHight
FEATURE [Sketcher::SketchObject] Sketch049  label="MaxPetalBase007"
  FullyConstrained = false
  MapMode = 5
  Placement = pos=(0,0,0) rot=(0.57735,0.57735,0.57735;2.0944rad)
  Support = -> [YZ_Plane020]
  expr: Constraints[0] = Spreadsheet.mmAxisTubeDia + 2 * Spreadsheet.mmFixatorThick - <<Spreadsheet>>.mmAirSpace / 2
  expr: Constraints[10] = Spreadsheet.mmAxisTubeDia
  expr: Constraints[12] = Spreadsheet.mmPetalPocketWidth - <<Spreadsheet>>.mmAirSpace / 2
  expr: Constraints[1] = Spreadsheet.mmAxisTubeDia
  expr: Constraints[6] = Spreadsheet.mmAxisTubeDia / 2 + Spreadsheet.mmPetalHightMax - <<Spreadsheet>>.mmAirSpace
  sketch-geometry (7):
    g0: Circle CenterX=0 CenterY=-1.8e-15 CenterZ=0 NormalX=0 NormalY=0 NormalZ=1 AngleXU=0 Radius=39.855
    g1: Circle CenterX=0 CenterY=-1.8e-15 CenterZ=0 NormalX=0 NormalY=0 NormalZ=1 AngleXU=0 Radius=26.42
    g2: ArcOfCircle CenterX=0 CenterY=-1.8e-15 CenterZ=0 NormalX=0 NormalY=0 NormalZ=1 AngleXU=0 Radius=20.4 StartAngle=5.86056 EndAngle=6.76902
    g3: LineSegment StartX=19.6502 StartY=5.47991 StartZ=0 EndX=25.72 EndY=5.47991 EndZ=0
    g4: LineSegment StartX=25.72 StartY=5.47991 StartZ=0 EndX=25.72 EndY=-5.47991 EndZ=0
    g5: LineSegment StartX=25.72 StartY=-5.47991 StartZ=0 EndX=19.6502 EndY=-5.47991 EndZ=0
    g6: ArcOfCircle CenterX=0 CenterY=-1.8e-15 CenterZ=0 NormalX=0 NormalY=0 NormalZ=1 AngleXU=0 Radius=20.4 StartAngle=6.01122 EndAngle=6.55515
  constraints (17):
    c: Diameter(g1) = 52.84
    c: Diameter(g2) = 40.8
    c: Coincident(g3,g4)
    c: Coincident(g4,g5)
    c: Coincident(g0,g2)
    c: Vertical(g4)
    c: DistanceX(g-1,g4) = 25.72
    c: Coincident(g6,g0)
    c: Coincident(g6,g3)
    c: Coincident(g6,g5)
    c: Diameter(g6) = 40.8
    c: Symmetric(g3,g5,g-1)
    c: DistanceY(g5,g3) = 10.9598
    c: Horizontal(g3)
    c: Horizontal(g5)
    c: Coincident(g1,g6)
    c: Coincident(g-1,g6)
FEATURE [Sketcher::SketchObject] Sketch050  label="MinPetalBase006"
  AttachmentOffset = pos=(0,0,17.36) rot=(0,0,1;0rad)
  FullyConstrained = false
  MapMode = 5
  Placement = pos=(17.36,-3.9e-15,3.9e-15) rot=(0.57735,0.57735,0.57735;2.0944rad)
  Support = -> [YZ_Plane020]
  expr: .AttachmentOffset.Base.z = Spreadsheet.mmFixatorHight * 0.9 - 1
  expr: Constraints[0] = Spreadsheet.mmAxisTubeDia + 2 * Spreadsheet.mmFixatorThick
  expr: Constraints[10] = Spreadsheet.mmAxisTubeDia
  expr: Constraints[12] = Spreadsheet.mmPetalPocketWidth - <<Spreadsheet>>.mmAirSpace / 2
  expr: Constraints[1] = Spreadsheet.mmAxisTubeDia
  expr: Constraints[6] = Spreadsheet.mmAxisTubeDia / 2 + Spreadsheet.mmPetalHightMin - <<Spreadsheet>>.mmAirSpace / 2
  sketch-geometry (7):
    g0: Circle CenterX=0 CenterY=-1.9e-15 CenterZ=0 NormalX=0 NormalY=0 NormalZ=1 AngleXU=0 Radius=39.844
    g1: Circle CenterX=0 CenterY=-1.9e-15 CenterZ=0 NormalX=0 NormalY=0 NormalZ=1 AngleXU=0 Radius=26.62
    g2: ArcOfCircle CenterX=0 CenterY=-1.9e-15 CenterZ=0 NormalX=0 NormalY=0 NormalZ=1 AngleXU=0 Radius=20.4 StartAngle=3.89517 EndAngle=6.7757
    g3: LineSegment StartX=19.6502 StartY=5.47991 StartZ=0 EndX=23.06 EndY=5.47991 EndZ=0
    g4: LineSegment StartX=23.06 StartY=5.47991 StartZ=0 EndX=23.06 EndY=-5.47991 EndZ=0
    g5: LineSegment StartX=23.06 StartY=-5.47991 StartZ=0 EndX=19.6502 EndY=-5.47991 EndZ=0
    g6: ArcOfCircle CenterX=0 CenterY=-1.9e-15 CenterZ=0 NormalX=0 NormalY=0 NormalZ=1 AngleXU=0 Radius=20.4 StartAngle=6.01122 EndAngle=6.55515
  constraints (17):
    c: Diameter(g1) = 53.24
    c: Diameter(g2) = 40.8
    c: Coincident(g3,g4)
    c: Coincident(g4,g5)
    c: Coincident(g0,g2)
    c: Vertical(g4)
    c: DistanceX(g-1,g4) = 23.06
    c: Coincident(g6,g0)
    c: Coincident(g6,g3)
    c: Coincident(g6,g5)
    c: Diameter(g6) = 40.8
    c: Symmetric(g3,g5,g-1)
    c: DistanceY(g5,g3) = 10.9598
    c: Horizontal(g5)
    c: Horizontal(g3)
    c: Coincident(g1,g6)
    c: Coincident(g-1,g6)
FEATURE [PartDesign::AdditiveLoft] AdditiveLoft001
  BaseFeature = -> Pad015
  Closed = false
  Placement = pos=(0,0,0) rot=(0.57735,0.57735,0.57735;2.0944rad)
  Profile = -> Sketch049
  Refine = true
  Ruled = false
  Sections = -> [Sketch050]
FEATURE [Sketcher::SketchObject] Sketch051  label="CommonFixatorScatch005"
  FullyConstrained = false
  MapMode = 5
  Placement = pos=(0,0,0) rot=(0.57735,0.57735,0.57735;2.0944rad)
  Support = -> [YZ_Plane020]
  expr: Constraints[0] = Spreadsheet.mmAxisTubeDia + 2 * Spreadsheet.mmFixatorThick - Spreadsheet.mmAirSpace
  expr: Constraints[18] = <<Spreadsheet>>.mmAxisTubeDia
  expr: Constraints[23] = Spreadsheet.mmPetalPocketWidth - <<Spreadsheet>>.mmAirSpace / 2
  sketch-geometry (9):
    g0: Circle CenterX=0 CenterY=0 CenterZ=0 NormalX=0 NormalY=0 NormalZ=1 AngleXU=0 Radius=26.22
    g1: LineSegment StartX=0 StartY=0 StartZ=0 EndX=32.909 EndY=19 EndZ=0
    g2: LineSegment StartX=0 StartY=0 StartZ=0 EndX=19.9273 EndY=-34.515 EndZ=0
    g3: ArcOfCircle CenterX=0 CenterY=0 CenterZ=0 NormalX=0 NormalY=0 NormalZ=1 AngleXU=0 Radius=20.4 StartAngle=4.71239 EndAngle=6.80678
    g4: LineSegment StartX=0 StartY=-38 StartZ=0 EndX=0 EndY=0 EndZ=0
    g5: LineSegment StartX=5.07936 StartY=-19.7575 StartZ=0 EndX=8.07474 EndY=-24.9457 EndZ=0
    g6: LineSegment StartX=8.07474 StartY=-24.9457 StartZ=0 EndX=17.5662 EndY=-19.4658 EndZ=0
    g7: LineSegment StartX=17.5662 StartY=-19.4658 StartZ=0 EndX=14.5708 EndY=-14.2776 EndZ=0
    g8: ArcOfCircle CenterX=0 CenterY=0 CenterZ=0 NormalX=0 NormalY=0 NormalZ=1 AngleXU=0 Radius=20.4 StartAngle=4.96402 EndAngle=5.50795
  constraints (24):
    c: Diameter(g0) = 52.44
    c: Angle(g-1,g1) = 0.523599
    c: PointOnObject(g4,g-2)
    c: Angle(g2,g-1) = 1.0472
    c: Coincident(g-1,g0)
    c: PointOnObject(g3,g1)
    c: Coincident(g4,g2)
    c: Equal(g4,g1)
    c: Coincident(g5,g6)
    c: Coincident(g6,g7)
    c: Symmetric(g5,g7,g2)
    c: Parallel(g7,g5)
    c: Perpendicular(g6,g7)
    c: PointOnObject(g6,g0)
    c: PointOnObject(g5,g0)
    c: Coincident(g1,g2)
    c: Coincident(g1,g0)
    c: Coincident(g3,g0)
    c: Diameter(g3) = 40.8
    c: PointOnObject(g5,g3)
    c: Coincident(g8,g0)
    c: Coincident(g8,g5)
    c: PointOnObject(g8,g7)
    c: Distance(g7,g5) = 10.9598
FEATURE [PartDesign::Pad] Pad016
  BaseFeature = -> AdditiveLoft001
  Direction = (1,-2e-16,3e-16)
  Length = 20.4
  Length2 = 10
  Placement = pos=(0,0,0) rot=(0.57735,0.57735,0.57735;2.0944rad)
  Profile = -> Sketch051
  ReferenceAxis = -> Sketch051 [N_Axis]
  Refine = true
  Type = 0
  expr: Length = <<Spreadsheet>>.mmFixatorHight
FEATURE [Sketcher::SketchObject] Sketch052
  FullyConstrained = false
  MapMode = 5
  Support = -> [XY_Plane020]
  expr: Constraints[13] = 2 * <<Spreadsheet>>.mmFixatorHight
  expr: Constraints[14] = <<Spreadsheet>>.mmAxisTubeDia / 2 + 5
  expr: Constraints[17] = Spreadsheet.mmAxisTubeDia
  sketch-geometry (7):
    g0: LineSegment StartX=-40.8 StartY=27.4 StartZ=0 EndX=-38.8 EndY=27.4 EndZ=0
    g1: LineSegment StartX=-38.8 StartY=27.4 StartZ=0 EndX=-38.8 EndY=25.4 EndZ=0
    g2: LineSegment StartX=-38.8 StartY=25.4 StartZ=0 EndX=-16.8 EndY=25.4 EndZ=0
    g3: LineSegment StartX=-16.8 StartY=25.4 StartZ=0 EndX=-5 EndY=37.2 EndZ=0
    g4: LineSegment StartX=-5 StartY=37.2 StartZ=0 EndX=-5 EndY=63.2 EndZ=0
    g5: LineSegment StartX=-5 StartY=63.2 StartZ=0 EndX=-40.8 EndY=63.2 EndZ=0
    g6: LineSegment StartX=-40.8 StartY=63.2 StartZ=0 EndX=-40.8 EndY=27.4 EndZ=0
  constraints (21):
    c: Horizontal(g0)
    c: Coincident(g0,g1)
    c: Vertical(g1)
    c: Coincident(g1,g2)
    c: Horizontal(g2)
    c: Coincident(g3,g4)
    c: Vertical(g4)
    c: Coincident(g4,g5)
    c: Horizontal(g5)
    c: Coincident(g5,g6)
    c: Coincident(g6,g0)
    c: Vertical(g6)
    c: DistanceX(g4,g-1) = 5
    c: DistanceX(g5,g-1) = 40.8
    c: DistanceY(g-1,g2) = 25.4
    c: DistanceX(g0,g0) = 2
    c: DistanceX(g2,g2) = 22
    c: DistanceY(g6,g6) = 40.8
    c: Coincident(g3,g2)
    c: DistanceY(g1,g1) = 2
    c: Angle(g-1,g3) = 0.785398
FEATURE [PartDesign::Groove] Groove
  Angle = 360
  Axis = (1,0,0)
  Base = (0,0,0)
  BaseFeature = -> Pad016
  Placement = pos=(0,0,0) rot=(0.57735,0.57735,0.57735;2.0944rad)
  Profile = -> Sketch052
  ReferenceAxis = -> X_Axis020
  Refine = true
  Reversed = true
FEATURE [Sketcher::SketchObject] Sketch053  label="CommonFixatorScatch006"
  AttachmentOffset = pos=(0,0,-7) rot=(0,0,1;0rad)
  FullyConstrained = false
  MapMode = 5
  Placement = pos=(-7,1.6e-15,-1.6e-15) rot=(0.57735,0.57735,0.57735;2.0944rad)
  Support = -> [YZ_Plane020]
  expr: Constraints[0] = Spreadsheet.mmAxisTubeDia + 2 * Spreadsheet.mmFixatorThick + 2 * Spreadsheet.mmTwoSideTapeThick
  expr: Constraints[13] = <<Spreadsheet>>.mmAxisTubeDia
  expr: Constraints[15] = <<Spreadsheet>>.mmAirSpace
  expr: Constraints[9] = Spreadsheet.mmBaseWidth
  sketch-geometry (20):
    g0: Circle CenterX=0 CenterY=0 CenterZ=0 NormalX=0 NormalY=0 NormalZ=1 AngleXU=0 Radius=26.72
    g1: LineSegment StartX=0 StartY=0 StartZ=0 EndX=33.9 EndY=19.5722 EndZ=0
    g2: LineSegment StartX=-3.7e-15 StartY=-20.4 StartZ=0 EndX=-3.7e-15 EndY=-39.1443 EndZ=0
    g3: LineSegment StartX=-3.7e-15 StartY=-39.1443 StartZ=0 EndX=6.1902 EndY=-42.7183 EndZ=0
    g4: LineSegment StartX=6.1902 StartY=-42.7183 StartZ=0 EndX=40.0902 EndY=15.9983 EndZ=0
    g5: ArcOfCircle CenterX=0 CenterY=0 CenterZ=0 NormalX=0 NormalY=0 NormalZ=1 AngleXU=0 Radius=20.4 StartAngle=4.71239 EndAngle=6.76756
    g6: LineSegment StartX=0 StartY=0 StartZ=0 EndX=20.0617 EndY=-34.7479 EndZ=0
    g7: LineSegment StartX=33.9 StartY=19.5722 StartZ=0 EndX=40.0902 EndY=15.9983 EndZ=0
    g8: ArcOfCircle CenterX=0 CenterY=0 CenterZ=0 NormalX=0 NormalY=0 NormalZ=1 AngleXU=0 Radius=20.4 StartAngle=4.71239 EndAngle=6.80678
    g9: LineSegment StartX=17.6669 StartY=10.2 StartZ=0 EndX=33.9 EndY=19.5722 EndZ=0
    g10: LineSegment StartX=-3.7e-15 StartY=-39.1443 StartZ=0 EndX=0 EndY=0 EndZ=0
    g11: LineSegment StartX=34.7 StartY=19.1103 StartZ=0 EndX=40.0902 EndY=15.9983 EndZ=0
    g12: Circle CenterX=29.0138 CenterY=9.45344 CenterZ=0 NormalX=0 NormalY=0 NormalZ=1 AngleXU=0 Radius=4.5
    g13: Circle CenterX=6.32 CenterY=-29.8534 CenterZ=0 NormalX=0 NormalY=0 NormalZ=1 AngleXU=0 Radius=4.5
    g14: LineSegment StartX=6.32 StartY=-29.8534 StartZ=0 EndX=29.0138 EndY=9.45344 EndZ=0
    g15: LineSegment StartX=0 StartY=0 StartZ=0 EndX=17.6669 EndY=-10.2 EndZ=0
    g16: LineSegment StartX=6.32 StartY=-29.8534 StartZ=0 EndX=0 EndY=-29.8534 EndZ=0
    g17: LineSegment StartX=6.32 StartY=-29.8534 StartZ=0 EndX=11.7933 EndY=-33.0134 EndZ=0
    g18: LineSegment StartX=29.0138 StartY=9.45344 StartZ=0 EndX=25.8538 EndY=14.9267 EndZ=0
    g19: LineSegment StartX=29.0138 StartY=9.45344 StartZ=0 EndX=34.4871 EndY=6.29344 EndZ=0
  constraints (53):
    c: Diameter(g0) = 53.44
    c: Angle(g-1,g1) = 0.523599
    c: Vertical(g2)
    c: Coincident(g2,g3)
    c: Coincident(g3,g4)
    c: PointOnObject(g2,g-2)
    c: Perpendicular(g4,g3)
    c: Tangent(g0,g4)
    c: Angle(g6,g-1) = 1.0472
    c: Distance(g3,g4) = 67.8
    c: Coincident(g-1,g0)
    c: Coincident(g5,g0)
    c: Coincident(g5,g2)
    c: Diameter(g5) = 40.8
    c: Coincident(g1,g5)
    c: Distance(g11,g1) = 0.8
    c: Perpendicular(g7,g4)
    c: Coincident(g7,g4)
    c: PointOnObject(g11,g7)
    c: Coincident(g8,g5)
    c: Coincident(g8,g2)
    c: PointOnObject(g8,g1)
    c: Coincident(g9,g8)
    c: Coincident(g9,g7)
    c: Coincident(g1,g7)
    c: Coincident(g10,g2)
    c: Coincident(g10,g6)
    c: Equal(g10,g1)
    c: Coincident(g6,g5)
    c: Equal(g3,g7)
    c: Coincident(g11,g4)
    c: Equal(g13,g12)
    c: Diameter(g12) = 9
    c: Coincident(g14,g13)
    c: Coincident(g14,g12)
    c: Tangent(g14,g5)
    c: Parallel(g14,g4)
    c: Coincident(g15,g5)
    c: PointOnObject(g15,g5)
    c: Symmetric(g13,g12,g15)
    c: Coincident(g16,g13)
    c: PointOnObject(g16,g2)
    c: Coincident(g17,g13)
    c: PointOnObject(g17,g4)
    c: Coincident(g18,g12)
    c: PointOnObject(g18,g1)
    c: Coincident(g19,g12)
    c: PointOnObject(g19,g4)
    c: Perpendicular(g4,g19)
    c: Equal(g17,g16)
    c: Perpendicular(g4,g17)
    c: Perpendicular(g10,g16)
    c: Perpendicular(g1,g18)
FEATURE [Sketcher::SketchObject] Sketch054  label="CommonFixatorScatch007"
  AttachmentOffset = pos=(0,0,20.4) rot=(0,0,1;0rad)
  FullyConstrained = false
  MapMode = 5
  Placement = pos=(20.4,-4.5e-15,4.5e-15) rot=(0.57735,0.57735,0.57735;2.0944rad)
  Support = -> [YZ_Plane020]
  expr: .AttachmentOffset.Base.z = <<Spreadsheet>>.mmFixatorHight
  expr: Constraints[0] = Spreadsheet.mmAxisTubeDia + 2 * Spreadsheet.mmFixatorThick + 2 * Spreadsheet.mmTwoSideTapeThick
  expr: Constraints[13] = <<Spreadsheet>>.mmAxisTubeDia
  expr: Constraints[15] = <<Spreadsheet>>.mmAirSpace
  expr: Constraints[36] = 2.2 + <<Spreadsheet>>.mmAirSpace / 2
  expr: Constraints[37] = <<Spreadsheet>>.mmAxisTubeDia / 2 + 2.19 / 2 + 1.2
  expr: Constraints[38] = <<Spreadsheet>>.mmAxisTubeDia / 2 + 2.19 / 2 + 1.2
  expr: Constraints[9] = Spreadsheet.mmBaseWidth
  sketch-geometry (15):
    g0: Circle CenterX=0 CenterY=0 CenterZ=0 NormalX=0 NormalY=0 NormalZ=1 AngleXU=0 Radius=26.72
    g1: LineSegment StartX=0 StartY=0 StartZ=0 EndX=33.9 EndY=19.5722 EndZ=0
    g2: LineSegment StartX=-3.7e-15 StartY=-20.4 StartZ=0 EndX=-3.7e-15 EndY=-39.1443 EndZ=0
    g3: LineSegment StartX=-3.7e-15 StartY=-39.1443 StartZ=0 EndX=6.1902 EndY=-42.7183 EndZ=0
    g4: LineSegment StartX=6.1902 StartY=-42.7183 StartZ=0 EndX=40.0902 EndY=15.9983 EndZ=0
    g5: ArcOfCircle CenterX=0 CenterY=0 CenterZ=0 NormalX=0 NormalY=0 NormalZ=1 AngleXU=0 Radius=20.4 StartAngle=4.71239 EndAngle=6.76621
    g6: LineSegment StartX=0 StartY=0 StartZ=0 EndX=20.0576 EndY=-34.7407 EndZ=0
    g7: LineSegment StartX=33.9 StartY=19.5722 StartZ=0 EndX=40.0902 EndY=15.9983 EndZ=0
    g8: ArcOfCircle CenterX=0 CenterY=0 CenterZ=0 NormalX=0 NormalY=0 NormalZ=1 AngleXU=0 Radius=20.4 StartAngle=4.71239 EndAngle=6.80678
    g9: LineSegment StartX=17.6669 StartY=10.2 StartZ=0 EndX=33.9 EndY=19.5722 EndZ=0
    g10: LineSegment StartX=-3.7e-15 StartY=-39.1443 StartZ=0 EndX=0 EndY=0 EndZ=0
    g11: LineSegment StartX=34.7 StartY=19.1103 StartZ=0 EndX=40.0902 EndY=15.9983 EndZ=0
    g12: LineSegment StartX=0 StartY=0 StartZ=0 EndX=17.6864 EndY=-10.1661 EndZ=0
    g13: Circle CenterX=11.3475 CenterY=-19.6544 CenterZ=0 NormalX=0 NormalY=0 NormalZ=1 AngleXU=0 Radius=1.3
    g14: Circle CenterX=22.695 CenterY=0 CenterZ=0 NormalX=0 NormalY=0 NormalZ=1 AngleXU=0 Radius=1.3
  constraints (39):
    c: Diameter(g0) = 53.44
    c: Angle(g-1,g1) = 0.523599
    c: Vertical(g2)
    c: Coincident(g2,g3)
    c: Coincident(g3,g4)
    c: PointOnObject(g2,g-2)
    c: Perpendicular(g4,g3)
    c: Tangent(g0,g4)
    c: Angle(g6,g-1) = 1.0472
    c: Distance(g3,g4) = 67.8
    c: Coincident(g-1,g0)
    c: Coincident(g5,g0)
    c: Coincident(g5,g2)
    c: Diameter(g5) = 40.8
    c: Coincident(g1,g5)
    c: Distance(g11,g1) = 0.8
    c: Perpendicular(g7,g4)
    c: Coincident(g7,g4)
    c: PointOnObject(g11,g7)
    c: Coincident(g8,g5)
    c: Coincident(g8,g2)
    c: PointOnObject(g8,g1)
    c: Coincident(g9,g8)
    c: Coincident(g9,g7)
    c: Coincident(g1,g7)
    c: Coincident(g10,g2)
    c: Coincident(g10,g6)
    c: Equal(g10,g1)
    c: Coincident(g6,g5)
    c: Equal(g3,g7)
    c: Coincident(g11,g4)
    c: Coincident(g12,g5)
    c: PointOnObject(g12,g5)
    c: PointOnObject(g13,g6)
    c: PointOnObject(g14,g-1)
    c: Equal(g13,g14)
    c: Diameter(g13) = 2.6
    c: DistanceX(g-1,g14) = 22.695
    c: Distance(g13,g0) = 22.695
FEATURE [PartDesign::Pocket] Pocket006
  BaseFeature = -> Groove
  Direction = (-1,2e-16,-3e-16)
  Length = 41
  Length2 = 5
  Placement = pos=(0,0,0) rot=(0.57735,0.57735,0.57735;2.0944rad)
  Profile = -> Sketch054
  ReferenceAxis = -> Sketch054 [N_Axis]
  Refine = true
  Type = 0
FEATURE [PartDesign::Fillet] Fillet001
  Base = -> Pocket006
  BaseFeature = -> Pocket006
  Placement = pos=(0,0,0) rot=(0.57735,0.57735,0.57735;2.0944rad)
  Radius = 1
  Refine = true
  SupportTransform = false
  UseAllEdges = false
FEATURE [PartDesign::Pocket] Pocket007
  BaseFeature = -> Fillet001
  Direction = (-1,2e-16,-3e-16)
  Length = 27
  Length2 = 5
  Placement = pos=(0,0,0) rot=(0.57735,0.57735,0.57735;2.0944rad)
  Profile = -> Sketch053
  ReferenceAxis = -> Sketch053 [N_Axis]
  Refine = true
  Type = 0
FEATURE [PartDesign::Chamfer] Chamfer005
  Angle = 45
  Base = -> Pocket007 [Edge75,Edge27]
  BaseFeature = -> Pocket007
  ChamferType = 1
  FlipDirection = false
  Placement = pos=(0,0,0) rot=(0.57735,0.57735,0.57735;2.0944rad)
  Refine = true
  Size = 4
  Size2 = 4
  SupportTransform = false
  UseAllEdges = false
FEATURE [PartDesign::Chamfer] Chamfer006
  Angle = 45
  Base = -> Chamfer005 [Edge79,Edge77]
  BaseFeature = -> Chamfer005
  ChamferType = 0
  FlipDirection = false
  Placement = pos=(0,0,0) rot=(0.57735,0.57735,0.57735;2.0944rad)
  Refine = true
  Size = 2.4
  Size2 = 1
  SupportTransform = false
  UseAllEdges = false
FEATURE [PartDesign::Chamfer] Chamfer007
  Angle = 45
  Base = -> Chamfer006 [Edge31,Edge33,Edge34,Edge35,Edge32,Edge37,Edge42,Edge39,Edge38,Edge43,Edge36]
  BaseFeature = -> Chamfer006
  ChamferType = 0
  FlipDirection = false
  Placement = pos=(0,0,0) rot=(0.57735,0.57735,0.57735;2.0944rad)
  Refine = true
  Size = 1
  Size2 = 1
  SupportTransform = false
  UseAllEdges = false
FEATURE [PartDesign::Body] Body012  label="AxisBodyBandage001"
  Group = -> [Sketch048,Pad015,Sketch049,Sketch050,AdditiveLoft001,Sketch051,Pad016,Sketch052,Groove,Sketch054,Sketch053,Pocket006,Fillet001,Pocket007,Chamfer005,Chamfer006,Chamfer007]
  Origin = -> Origin024
  Tip = -> Chamfer007
COMPONENT P7 — recipe-attached ("PulleyBodyFixator", modeled in this document).
Construction recipe (the document's own serialized feature program — sketch geometry with constraints, then the solid features built on it; lengths are millimeters unless a unit is written):

FEATURE [Sketcher::SketchObject] Sketch055  label="CommonFixatorScatch008"
  FullyConstrained = false
  MapMode = 5
  Placement = pos=(0,0,0) rot=(0.57735,0.57735,0.57735;2.0944rad)
  Support = -> [YZ_Plane022]
  expr: Constraints[0] = Spreadsheet.mmAxisTubeDia + 2 * Spreadsheet.mmFixatorThick + 2 * Spreadsheet.mmTwoSideTapeThick
  expr: Constraints[25] = <<Spreadsheet>>.mmAirSpace
  expr: Constraints[8] = <<Spreadsheet>>.mmAxisTubeDia
  sketch-geometry (12):
    g0: Circle CenterX=0 CenterY=0 CenterZ=0 NormalX=0 NormalY=0 NormalZ=1 AngleXU=0 Radius=26.72
    g1: LineSegment StartX=0 StartY=0 StartZ=0 EndX=35.3103 EndY=20.3864 EndZ=0
    g2: LineSegment StartX=-3.7e-15 StartY=-20.4 StartZ=0 EndX=-3.7e-15 EndY=-40.7728 EndZ=0
    g3: ArcOfCircle CenterX=0 CenterY=0 CenterZ=0 NormalX=0 NormalY=0 NormalZ=1 AngleXU=0 Radius=20.4 StartAngle=4.71239 EndAngle=6.76756
    g4: LineSegment StartX=0 StartY=0 StartZ=0 EndX=20.0617 EndY=-34.7479 EndZ=0
    g5: ArcOfCircle CenterX=0 CenterY=0 CenterZ=0 NormalX=0 NormalY=0 NormalZ=1 AngleXU=0 Radius=20.4 StartAngle=4.71239 EndAngle=6.80678
    g6: LineSegment StartX=17.6669 StartY=10.2 StartZ=0 EndX=35.2827 EndY=20.3705 EndZ=0
    g7: LineSegment StartX=-3.7e-15 StartY=-40.7728 StartZ=0 EndX=0 EndY=0 EndZ=0
    g8: LineSegment StartX=0 StartY=0 StartZ=0 EndX=17.6669 EndY=-10.2 EndZ=0
    g9: ArcOfCircle CenterX=0 CenterY=0 CenterZ=0 NormalX=0 NormalY=0 NormalZ=1 AngleXU=0 Radius=26.72 StartAngle=4.71239 EndAngle=6.77684
    g10: LineSegment StartX=18.0533 StartY=9.49933 StartZ=0 EndX=23.5298 EndY=12.6612 EndZ=0
    g11: LineSegment StartX=-3.7e-15 StartY=-20.4 StartZ=0 EndX=-4.9e-15 EndY=-26.72 EndZ=0
  constraints (29):
    c: Diameter(g0) = 53.44
    c: Angle(g-1,g1) = 0.523599
    c: Vertical(g2)
    c: PointOnObject(g2,g-2)
    c: Angle(g4,g-1) = 1.0472
    c: Coincident(g-1,g0)
    c: Coincident(g3,g0)
    c: Coincident(g3,g2)
    c: Diameter(g3) = 40.8
    c: Coincident(g1,g3)
    c: Coincident(g5,g3)
    c: Coincident(g5,g2)
    c: PointOnObject(g5,g1)
    c: Coincident(g6,g5)
    c: Coincident(g7,g2)
    c: Coincident(g7,g4)
    c: Equal(g7,g1)
    c: Coincident(g4,g3)
    c: Coincident(g8,g3)
    c: PointOnObject(g8,g3)
    c: Coincident(g9,g3)
    c: PointOnObject(g9,g0)
    c: Coincident(g10,g3)
    c: Coincident(g9,g10)
    c: Parallel(g10,g1)
    c: Distance(g9,g1) = 0.8
    c: PointOnObject(g9,g7)
    c: Coincident(g11,g3)
    c: Coincident(g11,g9)
FEATURE [Sketcher::SketchObject] Sketch056  label="MaxPetalBase008"
  FullyConstrained = false
  MapMode = 5
  Placement = pos=(0,0,0) rot=(0.57735,0.57735,0.57735;2.0944rad)
  Support = -> [YZ_Plane022]
  expr: Constraints[0] = Spreadsheet.mmAxisTubeDia + 2 * Spreadsheet.mmFixatorThick - <<Spreadsheet>>.mmAirSpace / 2
  expr: Constraints[10] = Spreadsheet.mmAxisTubeDia
  expr: Constraints[12] = Spreadsheet.mmPetalPocketWidth - <<Spreadsheet>>.mmAirSpace / 2
  expr: Constraints[1] = Spreadsheet.mmAxisTubeDia
  expr: Constraints[6] = Spreadsheet.mmAxisTubeDia / 2 + Spreadsheet.mmPetalHightMax - <<Spreadsheet>>.mmAirSpace
  sketch-geometry (7):
    g0: Circle CenterX=0 CenterY=-1.8e-15 CenterZ=0 NormalX=0 NormalY=0 NormalZ=1 AngleXU=0 Radius=39.855
    g1: Circle CenterX=0 CenterY=-1.8e-15 CenterZ=0 NormalX=0 NormalY=0 NormalZ=1 AngleXU=0 Radius=26.42
    g2: ArcOfCircle CenterX=0 CenterY=-1.8e-15 CenterZ=0 NormalX=0 NormalY=0 NormalZ=1 AngleXU=0 Radius=20.4 StartAngle=5.86056 EndAngle=6.76902
    g3: LineSegment StartX=19.6502 StartY=5.47991 StartZ=0 EndX=25.72 EndY=5.47991 EndZ=0
    g4: LineSegment StartX=25.72 StartY=5.47991 StartZ=0 EndX=25.72 EndY=-5.47991 EndZ=0
    g5: LineSegment StartX=25.72 StartY=-5.47991 StartZ=0 EndX=19.6502 EndY=-5.47991 EndZ=0
    g6: ArcOfCircle CenterX=0 CenterY=-1.8e-15 CenterZ=0 NormalX=0 NormalY=0 NormalZ=1 AngleXU=0 Radius=20.4 StartAngle=6.01122 EndAngle=6.55515
  constraints (17):
    c: Diameter(g1) = 52.84
    c: Diameter(g2) = 40.8
    c: Coincident(g3,g4)
    c: Coincident(g4,g5)
    c: Coincident(g0,g2)
    c: Vertical(g4)
    c: DistanceX(g-1,g4) = 25.72
    c: Coincident(g6,g0)
    c: Coincident(g6,g3)
    c: Coincident(g6,g5)
    c: Diameter(g6) = 40.8
    c: Symmetric(g3,g5,g-1)
    c: DistanceY(g5,g3) = 10.9598
    c: Horizontal(g3)
    c: Horizontal(g5)
    c: Coincident(g1,g6)
    c: Coincident(g-1,g6)
FEATURE [Sketcher::SketchObject] Sketch057  label="MinPetalBase007"
  AttachmentOffset = pos=(0,0,17.36) rot=(0,0,1;0rad)
  FullyConstrained = false
  MapMode = 5
  Placement = pos=(17.36,-3.9e-15,3.9e-15) rot=(0.57735,0.57735,0.57735;2.0944rad)
  Support = -> [YZ_Plane022]
  expr: .AttachmentOffset.Base.z = Spreadsheet.mmFixatorHight * 0.9 - 1
  expr: Constraints[0] = Spreadsheet.mmAxisTubeDia + 2 * Spreadsheet.mmFixatorThick
  expr: Constraints[10] = Spreadsheet.mmAxisTubeDia
  expr: Constraints[12] = Spreadsheet.mmPetalPocketWidth - <<Spreadsheet>>.mmAirSpace / 2
  expr: Constraints[1] = Spreadsheet.mmAxisTubeDia
  expr: Constraints[6] = Spreadsheet.mmAxisTubeDia / 2 + Spreadsheet.mmPetalHightMin - <<Spreadsheet>>.mmAirSpace / 2
  sketch-geometry (7):
    g0: Circle CenterX=0 CenterY=-1.9e-15 CenterZ=0 NormalX=0 NormalY=0 NormalZ=1 AngleXU=0 Radius=39.844
    g1: Circle CenterX=0 CenterY=-1.9e-15 CenterZ=0 NormalX=0 NormalY=0 NormalZ=1 AngleXU=0 Radius=26.62
    g2: ArcOfCircle CenterX=0 CenterY=-1.9e-15 CenterZ=0 NormalX=0 NormalY=0 NormalZ=1 AngleXU=0 Radius=20.4 StartAngle=3.89517 EndAngle=6.7757
    g3: LineSegment StartX=19.6502 StartY=5.47991 StartZ=0 EndX=23.06 EndY=5.47991 EndZ=0
    g4: LineSegment StartX=23.06 StartY=5.47991 StartZ=0 EndX=23.06 EndY=-5.47991 EndZ=0
    g5: LineSegment StartX=23.06 StartY=-5.47991 StartZ=0 EndX=19.6502 EndY=-5.47991 EndZ=0
    g6: ArcOfCircle CenterX=0 CenterY=-1.9e-15 CenterZ=0 NormalX=0 NormalY=0 NormalZ=1 AngleXU=0 Radius=20.4 StartAngle=6.01122 EndAngle=6.55515
  constraints (17):
    c: Diameter(g1) = 53.24
    c: Diameter(g2) = 40.8
    c: Coincident(g3,g4)
    c: Coincident(g4,g5)
    c: Coincident(g0,g2)
    c: Vertical(g4)
    c: DistanceX(g-1,g4) = 23.06
    c: Coincident(g6,g0)
    c: Coincident(g6,g3)
    c: Coincident(g6,g5)
    c: Diameter(g6) = 40.8
    c: Symmetric(g3,g5,g-1)
    c: DistanceY(g5,g3) = 10.9598
    c: Horizontal(g5)
    c: Horizontal(g3)
    c: Coincident(g1,g6)
    c: Coincident(g-1,g6)
FEATURE [Sketcher::SketchObject] Sketch058
  FullyConstrained = false
  MapMode = 5
  Support = -> [XY_Plane022]
  expr: Constraints[13] = 28
  expr: Constraints[14] = <<Spreadsheet>>.mmAxisTubeDia / 2 + 5
  expr: Constraints[17] = Spreadsheet.mmAxisTubeDia
  sketch-geometry (7):
    g0: LineSegment StartX=-28 StartY=27.4 StartZ=0 EndX=-26 EndY=27.4 EndZ=0
    g1: LineSegment StartX=-26 StartY=27.4 StartZ=0 EndX=-26 EndY=25.4 EndZ=0
    g2: LineSegment StartX=-26 StartY=25.4 StartZ=0 EndX=-4 EndY=25.4 EndZ=0
    g3: LineSegment StartX=-4 StartY=25.4 StartZ=0 EndX=0 EndY=27.7094 EndZ=0
    g4: LineSegment StartX=0 StartY=27.7094 StartZ=0 EndX=0 EndY=63.2 EndZ=0
    g5: LineSegment StartX=0 StartY=63.2 StartZ=0 EndX=-28 EndY=63.2 EndZ=0
    g6: LineSegment StartX=-28 StartY=63.2 StartZ=0 EndX=-28 EndY=27.4 EndZ=0
  constraints (21):
    c: Horizontal(g0)
    c: Coincident(g0,g1)
    c: Vertical(g1)
    c: Coincident(g1,g2)
    c: Horizontal(g2)
    c: Coincident(g3,g4)
    c: Vertical(g4)
    c: Coincident(g4,g5)
    c: Horizontal(g5)
    c: Coincident(g5,g6)
    c: Coincident(g6,g0)
    c: Vertical(g6)
    c: DistanceX(g4,g-1) = 0
    c: DistanceX(g5,g-1) = 28
    c: DistanceY(g-1,g2) = 25.4
    c: DistanceX(g0,g0) = 2
    c: DistanceX(g2,g2) = 22
    c: DistanceY(g6,g6) = 40.8
    c: Coincident(g3,g2)
    c: DistanceY(g1,g1) = 2
    c: Angle(g-1,g3) = 0.523599
FEATURE [PartDesign::Pad] Pad017
  Direction = (1,-2e-16,3e-16)
  Length = 28
  Length2 = 10
  Placement = pos=(0,0,0) rot=(1,1,1;2.0944rad)
  Profile = -> Sketch055
  ReferenceAxis = -> Sketch055 [N_Axis]
  Refine = true
  Reversed = true
  Type = 0
FEATURE [PartDesign::AdditiveLoft] AdditiveLoft002
  BaseFeature = -> Pad017
  Closed = false
  Placement = pos=(0,0,0) rot=(1,1,1;2.0944rad)
  Profile = -> Sketch056
  Refine = true
  Ruled = false
  Sections = -> [Sketch057]
FEATURE [PartDesign::Groove] Groove001
  Angle = 360
  Axis = (1,0,0)
  Base = (0,0,0)
  BaseFeature = -> AdditiveLoft002
  Placement = pos=(0,0,0) rot=(1,1,1;2.0944rad)
  Profile = -> Sketch058
  ReferenceAxis = -> X_Axis022
  Refine = true
  Reversed = true
FEATURE [Sketcher::SketchObject] Sketch059  label="CommonFixatorScatch009"
  AttachmentOffset = pos=(0,0,20.4) rot=(0,0,1;0rad)
  FullyConstrained = false
  MapMode = 5
  Placement = pos=(20.4,-4.5e-15,4.5e-15) rot=(0.57735,0.57735,0.57735;2.0944rad)
  Support = -> [YZ_Plane022]
  expr: .AttachmentOffset.Base.z = <<Spreadsheet>>.mmFixatorHight
  expr: Constraints[0] = Spreadsheet.mmAxisTubeDia + 2 * Spreadsheet.mmFixatorThick + 2 * Spreadsheet.mmTwoSideTapeThick
  expr: Constraints[13] = <<Spreadsheet>>.mmAxisTubeDia
  expr: Constraints[15] = <<Spreadsheet>>.mmAirSpace
  expr: Constraints[34] = <<Spreadsheet>>.mmAxisTubeDia / 2 + 2.19 / 2 + 1.2
  expr: Constraints[35] = 2.2 + <<Spreadsheet>>.mmAirSpace / 2
  expr: Constraints[9] = Spreadsheet.mmBaseWidth
  sketch-geometry (14):
    g0: Circle CenterX=0 CenterY=0 CenterZ=0 NormalX=0 NormalY=0 NormalZ=1 AngleXU=0 Radius=26.72
    g1: LineSegment StartX=0 StartY=0 StartZ=0 EndX=33.9 EndY=19.5722 EndZ=0
    g2: LineSegment StartX=-3.7e-15 StartY=-20.4 StartZ=0 EndX=-3.7e-15 EndY=-39.1443 EndZ=0
    g3: LineSegment StartX=-3.7e-15 StartY=-39.1443 StartZ=0 EndX=6.1902 EndY=-42.7183 EndZ=0
    g4: LineSegment StartX=6.1902 StartY=-42.7183 StartZ=0 EndX=40.0902 EndY=15.9983 EndZ=0
    g5: ArcOfCircle CenterX=0 CenterY=0 CenterZ=0 NormalX=0 NormalY=0 NormalZ=1 AngleXU=0 Radius=20.4 StartAngle=4.71239 EndAngle=6.76621
    g6: LineSegment StartX=0 StartY=0 StartZ=0 EndX=20.0576 EndY=-34.7407 EndZ=0
    g7: LineSegment StartX=33.9 StartY=19.5722 StartZ=0 EndX=40.0902 EndY=15.9983 EndZ=0
    g8: ArcOfCircle CenterX=0 CenterY=0 CenterZ=0 NormalX=0 NormalY=0 NormalZ=1 AngleXU=0 Radius=20.4 StartAngle=4.71239 EndAngle=6.80678
    g9: LineSegment StartX=17.6669 StartY=10.2 StartZ=0 EndX=33.9 EndY=19.5722 EndZ=0
    g10: LineSegment StartX=-3.7e-15 StartY=-39.1443 StartZ=0 EndX=0 EndY=0 EndZ=0
    g11: LineSegment StartX=34.7 StartY=19.1103 StartZ=0 EndX=40.0902 EndY=15.9983 EndZ=0
    g12: LineSegment StartX=0 StartY=0 StartZ=0 EndX=17.6864 EndY=-10.1661 EndZ=0
    g13: Circle CenterX=22.695 CenterY=0 CenterZ=0 NormalX=0 NormalY=0 NormalZ=1 AngleXU=0 Radius=1.3
  constraints (36):
    c: Diameter(g0) = 53.44
    c: Angle(g-1,g1) = 0.523599
    c: Vertical(g2)
    c: Coincident(g2,g3)
    c: Coincident(g3,g4)
    c: PointOnObject(g2,g-2)
    c: Perpendicular(g4,g3)
    c: Tangent(g0,g4)
    c: Angle(g6,g-1) = 1.0472
    c: Distance(g3,g4) = 67.8
    c: Coincident(g-1,g0)
    c: Coincident(g5,g0)
    c: Coincident(g5,g2)
    c: Diameter(g5) = 40.8
    c: Coincident(g1,g5)
    c: Distance(g11,g1) = 0.8
    c: Perpendicular(g7,g4)
    c: Coincident(g7,g4)
    c: PointOnObject(g11,g7)
    c: Coincident(g8,g5)
    c: Coincident(g8,g2)
    c: PointOnObject(g8,g1)
    c: Coincident(g9,g8)
    c: Coincident(g9,g7)
    c: Coincident(g1,g7)
    c: Coincident(g10,g2)
    c: Coincident(g10,g6)
    c: Equal(g10,g1)
    c: Coincident(g6,g5)
    c: Equal(g3,g7)
    c: Coincident(g11,g4)
    c: Coincident(g12,g5)
    c: PointOnObject(g12,g5)
    c: PointOnObject(g13,g-1)
    c: DistanceX(g-1,g13) = 22.695
    c: Diameter(g13) = 2.6
FEATURE [PartDesign::Pocket] Pocket008
  BaseFeature = -> Groove001
  Direction = (-1,2e-16,-3e-16)
  Length = 48
  Length2 = 5
  Placement = pos=(0,0,0) rot=(1,1,1;2.0944rad)
  Profile = -> Sketch059
  ReferenceAxis = -> Sketch059 [N_Axis]
  Refine = true
  Type = 0
FEATURE [PartDesign::Body] Body013  label="PulletBodyFixator"
  Group = -> [Pad017,Sketch055,Sketch056,Sketch057,AdditiveLoft002,Sketch058,Groove001,Sketch059,Pocket008]
  Origin = -> Origin026
  Tip = -> Pocket008
